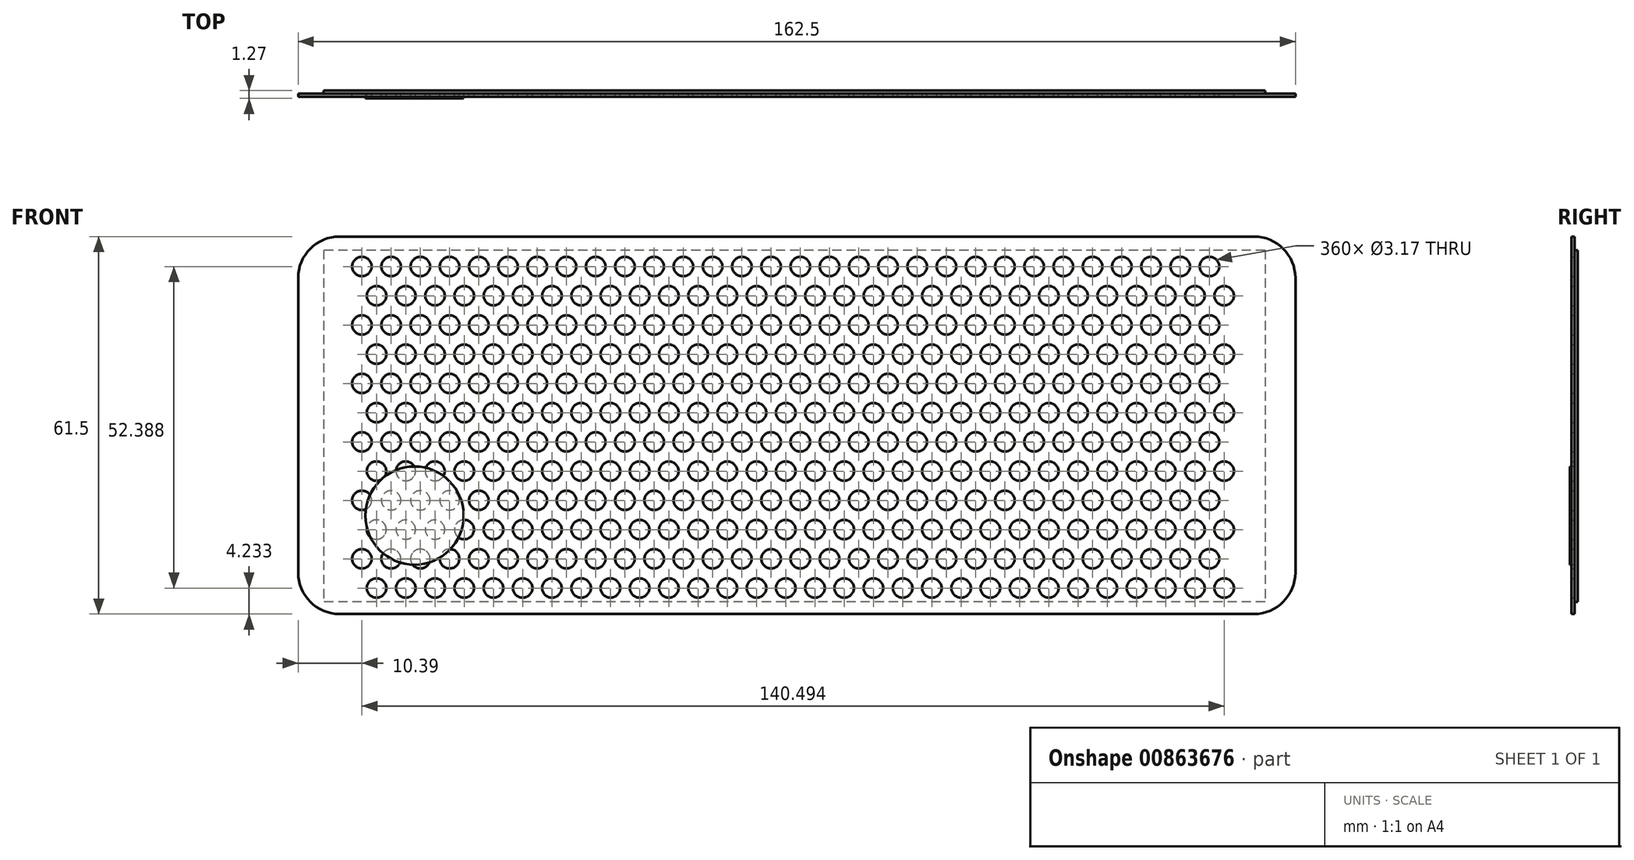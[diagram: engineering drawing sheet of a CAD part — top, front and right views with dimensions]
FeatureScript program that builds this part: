
annotation { "Feature Type Name" : "Feature", "Feature Type Description" : "" }
export const myFeature = defineFeature(function(context is Context, id is Id, definition is map)
    precondition{}
    {
        {
            var Q0;
            Q0=qCreatedBy(makeId("Front.planeOp"),FACE);
            var sketch = newSketch(context, id + "F0", { "sketchPlane" : qUnion([Q0])});
            skLineSegment(sketch, "E0.bottom", {"start": v(-73.44, 17) * mm, "end": v(75.54, 17) * mm});
            skLineSegment(sketch, "E0.top", {"start": v(-73.44, -44.5) * mm, "end": v(75.54, -44.5) * mm});
            skLineSegment(sketch, "E0.left", {"start": v(-80.2, 10.23) * mm, "end": v(-80.2, -37.75) * mm});
            skLineSegment(sketch, "E0.right", {"start": v(82.3, 10.23) * mm, "end": v(82.3, -37.75) * mm});
            skCircle(sketch, "E1", {"center": v(-69.81, 12.11) * mm, "radius": 1.59 * mm});
            skCircle(sketch, "E2.0.1.0", {"center": v(-69.81, 2.59) * mm, "radius": 1.59 * mm});
            skCircle(sketch, "E2.0.2.0", {"center": v(-69.81, -6.94) * mm, "radius": 1.59 * mm});
            skCircle(sketch, "E2.1.0.0", {"center": v(-65.05, 12.11) * mm, "radius": 1.59 * mm});
            skCircle(sketch, "E2.1.1.0", {"center": v(-65.05, 2.59) * mm, "radius": 1.59 * mm});
            skCircle(sketch, "E2.1.2.0", {"center": v(-65.05, -6.94) * mm, "radius": 1.59 * mm});
            skCircle(sketch, "E2.2.0.0", {"center": v(-60.29, 12.11) * mm, "radius": 1.59 * mm});
            skCircle(sketch, "E2.2.1.0", {"center": v(-60.29, 2.59) * mm, "radius": 1.59 * mm});
            skCircle(sketch, "E2.2.2.0", {"center": v(-60.29, -6.94) * mm, "radius": 1.59 * mm});
            skCircle(sketch, "E2.3.0.0", {"center": v(-55.52, 12.11) * mm, "radius": 1.59 * mm});
            skCircle(sketch, "E2.3.1.0", {"center": v(-55.52, 2.59) * mm, "radius": 1.59 * mm});
            skCircle(sketch, "E2.3.2.0", {"center": v(-55.52, -6.94) * mm, "radius": 1.59 * mm});
            skCircle(sketch, "E2.4.0.0", {"center": v(-50.76, 12.11) * mm, "radius": 1.59 * mm});
            skCircle(sketch, "E2.4.1.0", {"center": v(-50.76, 2.59) * mm, "radius": 1.59 * mm});
            skCircle(sketch, "E2.4.2.0", {"center": v(-50.76, -6.94) * mm, "radius": 1.59 * mm});
            skCircle(sketch, "E2.5.0.0", {"center": v(-46, 12.11) * mm, "radius": 1.59 * mm});
            skCircle(sketch, "E2.5.1.0", {"center": v(-46, 2.59) * mm, "radius": 1.59 * mm});
            skCircle(sketch, "E2.5.2.0", {"center": v(-46, -6.94) * mm, "radius": 1.59 * mm});
            skCircle(sketch, "E2.6.0.0", {"center": v(-41.24, 12.11) * mm, "radius": 1.59 * mm});
            skCircle(sketch, "E2.6.1.0", {"center": v(-41.24, 2.59) * mm, "radius": 1.59 * mm});
            skCircle(sketch, "E2.6.2.0", {"center": v(-41.24, -6.94) * mm, "radius": 1.59 * mm});
            skCircle(sketch, "E2.7.0.0", {"center": v(-36.47, 12.11) * mm, "radius": 1.59 * mm});
            skCircle(sketch, "E2.7.1.0", {"center": v(-36.47, 2.59) * mm, "radius": 1.59 * mm});
            skCircle(sketch, "E2.7.2.0", {"center": v(-36.47, -6.94) * mm, "radius": 1.59 * mm});
            skCircle(sketch, "E2.8.0.0", {"center": v(-31.71, 12.11) * mm, "radius": 1.59 * mm});
            skCircle(sketch, "E2.8.1.0", {"center": v(-31.71, 2.59) * mm, "radius": 1.59 * mm});
            skCircle(sketch, "E2.8.2.0", {"center": v(-31.71, -6.94) * mm, "radius": 1.59 * mm});
            skCircle(sketch, "E2.9.0.0", {"center": v(-26.95, 12.11) * mm, "radius": 1.59 * mm});
            skCircle(sketch, "E2.9.1.0", {"center": v(-26.95, 2.59) * mm, "radius": 1.59 * mm});
            skCircle(sketch, "E2.9.2.0", {"center": v(-26.95, -6.94) * mm, "radius": 1.59 * mm});
            skCircle(sketch, "E2.10.0.0", {"center": v(-22.19, 12.11) * mm, "radius": 1.59 * mm});
            skCircle(sketch, "E2.10.1.0", {"center": v(-22.19, 2.59) * mm, "radius": 1.59 * mm});
            skCircle(sketch, "E2.10.2.0", {"center": v(-22.19, -6.94) * mm, "radius": 1.59 * mm});
            skCircle(sketch, "E2.11.0.0", {"center": v(-17.42, 12.11) * mm, "radius": 1.59 * mm});
            skCircle(sketch, "E2.11.1.0", {"center": v(-17.42, 2.59) * mm, "radius": 1.59 * mm});
            skCircle(sketch, "E2.11.2.0", {"center": v(-17.42, -6.94) * mm, "radius": 1.59 * mm});
            skCircle(sketch, "E2.12.0.0", {"center": v(-12.66, 12.11) * mm, "radius": 1.59 * mm});
            skCircle(sketch, "E2.12.1.0", {"center": v(-12.66, 2.59) * mm, "radius": 1.59 * mm});
            skCircle(sketch, "E2.12.2.0", {"center": v(-12.66, -6.94) * mm, "radius": 1.59 * mm});
            skCircle(sketch, "E2.13.0.0", {"center": v(-7.9, 12.11) * mm, "radius": 1.59 * mm});
            skCircle(sketch, "E2.13.1.0", {"center": v(-7.9, 2.59) * mm, "radius": 1.59 * mm});
            skCircle(sketch, "E2.13.2.0", {"center": v(-7.9, -6.94) * mm, "radius": 1.59 * mm});
            skCircle(sketch, "E2.14.0.0", {"center": v(-3.14, 12.11) * mm, "radius": 1.59 * mm});
            skCircle(sketch, "E2.14.1.0", {"center": v(-3.14, 2.59) * mm, "radius": 1.59 * mm});
            skCircle(sketch, "E2.14.2.0", {"center": v(-3.14, -6.94) * mm, "radius": 1.59 * mm});
            skCircle(sketch, "E2.15.0.0", {"center": v(1.63, 12.11) * mm, "radius": 1.59 * mm});
            skCircle(sketch, "E2.15.1.0", {"center": v(1.63, 2.59) * mm, "radius": 1.59 * mm});
            skCircle(sketch, "E2.15.2.0", {"center": v(1.63, -6.94) * mm, "radius": 1.59 * mm});
            skCircle(sketch, "E2.16.0.0", {"center": v(6.39, 12.11) * mm, "radius": 1.59 * mm});
            skCircle(sketch, "E2.16.1.0", {"center": v(6.39, 2.59) * mm, "radius": 1.59 * mm});
            skCircle(sketch, "E2.16.2.0", {"center": v(6.39, -6.94) * mm, "radius": 1.59 * mm});
            skCircle(sketch, "E2.17.0.0", {"center": v(11.15, 12.11) * mm, "radius": 1.59 * mm});
            skCircle(sketch, "E2.17.1.0", {"center": v(11.15, 2.59) * mm, "radius": 1.59 * mm});
            skCircle(sketch, "E2.17.2.0", {"center": v(11.15, -6.94) * mm, "radius": 1.59 * mm});
            skCircle(sketch, "E2.18.0.0", {"center": v(15.91, 12.11) * mm, "radius": 1.59 * mm});
            skCircle(sketch, "E2.18.1.0", {"center": v(15.91, 2.59) * mm, "radius": 1.59 * mm});
            skCircle(sketch, "E2.18.2.0", {"center": v(15.91, -6.94) * mm, "radius": 1.59 * mm});
            skCircle(sketch, "E2.19.0.0", {"center": v(20.68, 12.11) * mm, "radius": 1.59 * mm});
            skCircle(sketch, "E2.19.1.0", {"center": v(20.68, 2.59) * mm, "radius": 1.59 * mm});
            skCircle(sketch, "E2.19.2.0", {"center": v(20.68, -6.94) * mm, "radius": 1.59 * mm});
            skLineSegment(sketch, "E2.direction1", {"start": v(-69.81, 12.11) * mm, "end": v(-65.05, 12.11) * mm, "construction": true});
            skLineSegment(sketch, "E2.direction2", {"start": v(-69.81, 12.11) * mm, "end": v(-69.81, 2.59) * mm, "construction": true});
            skCircle(sketch, "E3.0.20.0", {"center": v(25.44, 12.11) * mm, "radius": 1.59 * mm});
            skCircle(sketch, "E3.0.20.1", {"center": v(25.44, 2.59) * mm, "radius": 1.59 * mm});
            skCircle(sketch, "E3.0.20.2", {"center": v(25.44, -6.94) * mm, "radius": 1.59 * mm});
            skCircle(sketch, "E3.0.21.0", {"center": v(30.2, 12.11) * mm, "radius": 1.59 * mm});
            skCircle(sketch, "E3.0.21.1", {"center": v(30.2, 2.59) * mm, "radius": 1.59 * mm});
            skCircle(sketch, "E3.0.21.2", {"center": v(30.2, -6.94) * mm, "radius": 1.59 * mm});
            skCircle(sketch, "E3.0.22.0", {"center": v(34.96, 12.11) * mm, "radius": 1.59 * mm});
            skCircle(sketch, "E3.0.22.1", {"center": v(34.96, 2.59) * mm, "radius": 1.59 * mm});
            skCircle(sketch, "E3.0.22.2", {"center": v(34.96, -6.94) * mm, "radius": 1.59 * mm});
            skCircle(sketch, "E3.0.23.0", {"center": v(39.73, 12.11) * mm, "radius": 1.59 * mm});
            skCircle(sketch, "E3.0.23.1", {"center": v(39.73, 2.59) * mm, "radius": 1.59 * mm});
            skCircle(sketch, "E3.0.23.2", {"center": v(39.73, -6.94) * mm, "radius": 1.59 * mm});
            skCircle(sketch, "E3.0.24.0", {"center": v(44.49, 12.11) * mm, "radius": 1.59 * mm});
            skCircle(sketch, "E3.0.24.1", {"center": v(44.49, 2.59) * mm, "radius": 1.59 * mm});
            skCircle(sketch, "E3.0.24.2", {"center": v(44.49, -6.94) * mm, "radius": 1.59 * mm});
            skCircle(sketch, "E3.0.25.0", {"center": v(49.25, 12.11) * mm, "radius": 1.59 * mm});
            skCircle(sketch, "E3.0.25.1", {"center": v(49.25, 2.59) * mm, "radius": 1.59 * mm});
            skCircle(sketch, "E3.0.25.2", {"center": v(49.25, -6.94) * mm, "radius": 1.59 * mm});
            skCircle(sketch, "E3.0.26.0", {"center": v(54.01, 12.11) * mm, "radius": 1.59 * mm});
            skCircle(sketch, "E3.0.26.1", {"center": v(54.01, 2.59) * mm, "radius": 1.59 * mm});
            skCircle(sketch, "E3.0.26.2", {"center": v(54.01, -6.94) * mm, "radius": 1.59 * mm});
            skCircle(sketch, "E3.0.27.0", {"center": v(58.78, 12.11) * mm, "radius": 1.59 * mm});
            skCircle(sketch, "E3.0.27.1", {"center": v(58.78, 2.59) * mm, "radius": 1.59 * mm});
            skCircle(sketch, "E3.0.27.2", {"center": v(58.78, -6.94) * mm, "radius": 1.59 * mm});
            skCircle(sketch, "E3.0.28.0", {"center": v(63.54, 12.11) * mm, "radius": 1.59 * mm});
            skCircle(sketch, "E3.0.28.1", {"center": v(63.54, 2.59) * mm, "radius": 1.59 * mm});
            skCircle(sketch, "E3.0.28.2", {"center": v(63.54, -6.94) * mm, "radius": 1.59 * mm});
            skCircle(sketch, "E3.0.29.0", {"center": v(68.3, 12.11) * mm, "radius": 1.59 * mm});
            skCircle(sketch, "E3.0.29.1", {"center": v(68.3, 2.59) * mm, "radius": 1.59 * mm});
            skCircle(sketch, "E3.0.29.2", {"center": v(68.3, -6.94) * mm, "radius": 1.59 * mm});
            skCircle(sketch, "E4", {"center": v(-67.43, 7.35) * mm, "radius": 1.59 * mm});
            skLineSegment(sketch, "E5", {"start": v(-65.05, 2.59) * mm, "end": v(-69.81, 12.11) * mm});
            skCircle(sketch, "E6.0.0.3", {"center": v(-69.81, -16.46) * mm, "radius": 1.59 * mm});
            skCircle(sketch, "E6.0.0.4", {"center": v(-69.81, -25.99) * mm, "radius": 1.59 * mm});
            skCircle(sketch, "E6.0.0.5", {"center": v(-69.81, -35.51) * mm, "radius": 1.59 * mm});
            skCircle(sketch, "E6.0.1.3", {"center": v(-65.05, -16.46) * mm, "radius": 1.59 * mm});
            skCircle(sketch, "E6.0.1.4", {"center": v(-65.05, -25.99) * mm, "radius": 1.59 * mm});
            skCircle(sketch, "E6.0.1.5", {"center": v(-65.05, -35.51) * mm, "radius": 1.59 * mm});
            skCircle(sketch, "E6.0.2.3", {"center": v(-60.29, -16.46) * mm, "radius": 1.59 * mm});
            skCircle(sketch, "E6.0.2.4", {"center": v(-60.29, -25.99) * mm, "radius": 1.59 * mm});
            skCircle(sketch, "E6.0.2.5", {"center": v(-60.29, -35.51) * mm, "radius": 1.59 * mm});
            skCircle(sketch, "E6.0.3.3", {"center": v(-55.52, -16.46) * mm, "radius": 1.59 * mm});
            skCircle(sketch, "E6.0.3.4", {"center": v(-55.52, -25.99) * mm, "radius": 1.59 * mm});
            skCircle(sketch, "E6.0.3.5", {"center": v(-55.52, -35.51) * mm, "radius": 1.59 * mm});
            skCircle(sketch, "E6.0.4.3", {"center": v(-50.76, -16.46) * mm, "radius": 1.59 * mm});
            skCircle(sketch, "E6.0.4.4", {"center": v(-50.76, -25.99) * mm, "radius": 1.59 * mm});
            skCircle(sketch, "E6.0.4.5", {"center": v(-50.76, -35.51) * mm, "radius": 1.59 * mm});
            skCircle(sketch, "E6.0.5.3", {"center": v(-46, -16.46) * mm, "radius": 1.59 * mm});
            skCircle(sketch, "E6.0.5.4", {"center": v(-46, -25.99) * mm, "radius": 1.59 * mm});
            skCircle(sketch, "E6.0.5.5", {"center": v(-46, -35.51) * mm, "radius": 1.59 * mm});
            skCircle(sketch, "E6.0.6.3", {"center": v(-41.24, -16.46) * mm, "radius": 1.59 * mm});
            skCircle(sketch, "E6.0.6.4", {"center": v(-41.24, -25.99) * mm, "radius": 1.59 * mm});
            skCircle(sketch, "E6.0.6.5", {"center": v(-41.24, -35.51) * mm, "radius": 1.59 * mm});
            skCircle(sketch, "E6.0.7.3", {"center": v(-36.47, -16.46) * mm, "radius": 1.59 * mm});
            skCircle(sketch, "E6.0.7.4", {"center": v(-36.47, -25.99) * mm, "radius": 1.59 * mm});
            skCircle(sketch, "E6.0.7.5", {"center": v(-36.47, -35.51) * mm, "radius": 1.59 * mm});
            skCircle(sketch, "E6.0.8.3", {"center": v(-31.71, -16.46) * mm, "radius": 1.59 * mm});
            skCircle(sketch, "E6.0.8.4", {"center": v(-31.71, -25.99) * mm, "radius": 1.59 * mm});
            skCircle(sketch, "E6.0.8.5", {"center": v(-31.71, -35.51) * mm, "radius": 1.59 * mm});
            skCircle(sketch, "E6.0.9.3", {"center": v(-26.95, -16.46) * mm, "radius": 1.59 * mm});
            skCircle(sketch, "E6.0.9.4", {"center": v(-26.95, -25.99) * mm, "radius": 1.59 * mm});
            skCircle(sketch, "E6.0.9.5", {"center": v(-26.95, -35.51) * mm, "radius": 1.59 * mm});
            skCircle(sketch, "E6.0.10.3", {"center": v(-22.19, -16.46) * mm, "radius": 1.59 * mm});
            skCircle(sketch, "E6.0.10.4", {"center": v(-22.19, -25.99) * mm, "radius": 1.59 * mm});
            skCircle(sketch, "E6.0.10.5", {"center": v(-22.19, -35.51) * mm, "radius": 1.59 * mm});
            skCircle(sketch, "E6.0.11.3", {"center": v(-17.42, -16.46) * mm, "radius": 1.59 * mm});
            skCircle(sketch, "E6.0.11.4", {"center": v(-17.42, -25.99) * mm, "radius": 1.59 * mm});
            skCircle(sketch, "E6.0.11.5", {"center": v(-17.42, -35.51) * mm, "radius": 1.59 * mm});
            skCircle(sketch, "E6.0.12.3", {"center": v(-12.66, -16.46) * mm, "radius": 1.59 * mm});
            skCircle(sketch, "E6.0.12.4", {"center": v(-12.66, -25.99) * mm, "radius": 1.59 * mm});
            skCircle(sketch, "E6.0.12.5", {"center": v(-12.66, -35.51) * mm, "radius": 1.59 * mm});
            skCircle(sketch, "E6.0.13.3", {"center": v(-7.9, -16.46) * mm, "radius": 1.59 * mm});
            skCircle(sketch, "E6.0.13.4", {"center": v(-7.9, -25.99) * mm, "radius": 1.59 * mm});
            skCircle(sketch, "E6.0.13.5", {"center": v(-7.9, -35.51) * mm, "radius": 1.59 * mm});
            skCircle(sketch, "E6.0.14.3", {"center": v(-3.14, -16.46) * mm, "radius": 1.59 * mm});
            skCircle(sketch, "E6.0.14.4", {"center": v(-3.14, -25.99) * mm, "radius": 1.59 * mm});
            skCircle(sketch, "E6.0.14.5", {"center": v(-3.14, -35.51) * mm, "radius": 1.59 * mm});
            skCircle(sketch, "E6.0.15.3", {"center": v(1.63, -16.46) * mm, "radius": 1.59 * mm});
            skCircle(sketch, "E6.0.15.4", {"center": v(1.63, -25.99) * mm, "radius": 1.59 * mm});
            skCircle(sketch, "E6.0.15.5", {"center": v(1.63, -35.51) * mm, "radius": 1.59 * mm});
            skCircle(sketch, "E6.0.16.3", {"center": v(6.39, -16.46) * mm, "radius": 1.59 * mm});
            skCircle(sketch, "E6.0.16.4", {"center": v(6.39, -25.99) * mm, "radius": 1.59 * mm});
            skCircle(sketch, "E6.0.16.5", {"center": v(6.39, -35.51) * mm, "radius": 1.59 * mm});
            skCircle(sketch, "E6.0.17.3", {"center": v(11.15, -16.46) * mm, "radius": 1.59 * mm});
            skCircle(sketch, "E6.0.17.4", {"center": v(11.15, -25.99) * mm, "radius": 1.59 * mm});
            skCircle(sketch, "E6.0.17.5", {"center": v(11.15, -35.51) * mm, "radius": 1.59 * mm});
            skCircle(sketch, "E6.0.18.3", {"center": v(15.91, -16.46) * mm, "radius": 1.59 * mm});
            skCircle(sketch, "E6.0.18.4", {"center": v(15.91, -25.99) * mm, "radius": 1.59 * mm});
            skCircle(sketch, "E6.0.18.5", {"center": v(15.91, -35.51) * mm, "radius": 1.59 * mm});
            skCircle(sketch, "E6.0.19.3", {"center": v(20.68, -16.46) * mm, "radius": 1.59 * mm});
            skCircle(sketch, "E6.0.19.4", {"center": v(20.68, -25.99) * mm, "radius": 1.59 * mm});
            skCircle(sketch, "E6.0.19.5", {"center": v(20.68, -35.51) * mm, "radius": 1.59 * mm});
            skCircle(sketch, "E6.0.20.3", {"center": v(25.44, -16.46) * mm, "radius": 1.59 * mm});
            skCircle(sketch, "E6.0.20.4", {"center": v(25.44, -25.99) * mm, "radius": 1.59 * mm});
            skCircle(sketch, "E6.0.20.5", {"center": v(25.44, -35.51) * mm, "radius": 1.59 * mm});
            skCircle(sketch, "E6.0.21.3", {"center": v(30.2, -16.46) * mm, "radius": 1.59 * mm});
            skCircle(sketch, "E6.0.21.4", {"center": v(30.2, -25.99) * mm, "radius": 1.59 * mm});
            skCircle(sketch, "E6.0.21.5", {"center": v(30.2, -35.51) * mm, "radius": 1.59 * mm});
            skCircle(sketch, "E6.0.22.3", {"center": v(34.96, -16.46) * mm, "radius": 1.59 * mm});
            skCircle(sketch, "E6.0.22.4", {"center": v(34.96, -25.99) * mm, "radius": 1.59 * mm});
            skCircle(sketch, "E6.0.22.5", {"center": v(34.96, -35.51) * mm, "radius": 1.59 * mm});
            skCircle(sketch, "E6.0.23.3", {"center": v(39.73, -16.46) * mm, "radius": 1.59 * mm});
            skCircle(sketch, "E6.0.23.4", {"center": v(39.73, -25.99) * mm, "radius": 1.59 * mm});
            skCircle(sketch, "E6.0.23.5", {"center": v(39.73, -35.51) * mm, "radius": 1.59 * mm});
            skCircle(sketch, "E6.0.24.3", {"center": v(44.49, -16.46) * mm, "radius": 1.59 * mm});
            skCircle(sketch, "E6.0.24.4", {"center": v(44.49, -25.99) * mm, "radius": 1.59 * mm});
            skCircle(sketch, "E6.0.24.5", {"center": v(44.49, -35.51) * mm, "radius": 1.59 * mm});
            skCircle(sketch, "E6.0.25.3", {"center": v(49.25, -16.46) * mm, "radius": 1.59 * mm});
            skCircle(sketch, "E6.0.25.4", {"center": v(49.25, -25.99) * mm, "radius": 1.59 * mm});
            skCircle(sketch, "E6.0.25.5", {"center": v(49.25, -35.51) * mm, "radius": 1.59 * mm});
            skCircle(sketch, "E6.0.26.3", {"center": v(54.01, -16.46) * mm, "radius": 1.59 * mm});
            skCircle(sketch, "E6.0.26.4", {"center": v(54.01, -25.99) * mm, "radius": 1.59 * mm});
            skCircle(sketch, "E6.0.26.5", {"center": v(54.01, -35.51) * mm, "radius": 1.59 * mm});
            skCircle(sketch, "E6.0.27.3", {"center": v(58.78, -16.46) * mm, "radius": 1.59 * mm});
            skCircle(sketch, "E6.0.27.4", {"center": v(58.78, -25.99) * mm, "radius": 1.59 * mm});
            skCircle(sketch, "E6.0.27.5", {"center": v(58.78, -35.51) * mm, "radius": 1.59 * mm});
            skCircle(sketch, "E6.0.28.3", {"center": v(63.54, -16.46) * mm, "radius": 1.59 * mm});
            skCircle(sketch, "E6.0.28.4", {"center": v(63.54, -25.99) * mm, "radius": 1.59 * mm});
            skCircle(sketch, "E6.0.28.5", {"center": v(63.54, -35.51) * mm, "radius": 1.59 * mm});
            skCircle(sketch, "E6.0.29.3", {"center": v(68.3, -16.46) * mm, "radius": 1.59 * mm});
            skCircle(sketch, "E6.0.29.4", {"center": v(68.3, -25.99) * mm, "radius": 1.59 * mm});
            skCircle(sketch, "E6.0.29.5", {"center": v(68.3, -35.51) * mm, "radius": 1.59 * mm});
            skCircle(sketch, "E7.0.1.0", {"center": v(-67.43, -2.18) * mm, "radius": 1.59 * mm});
            skCircle(sketch, "E7.0.2.0", {"center": v(-67.43, -11.7) * mm, "radius": 1.59 * mm});
            skCircle(sketch, "E7.0.3.0", {"center": v(-67.43, -21.23) * mm, "radius": 1.59 * mm});
            skCircle(sketch, "E7.0.4.0", {"center": v(-67.43, -30.75) * mm, "radius": 1.59 * mm});
            skCircle(sketch, "E7.0.5.0", {"center": v(-67.43, -40.28) * mm, "radius": 1.59 * mm});
            skCircle(sketch, "E7.1.0.0", {"center": v(-62.67, 7.35) * mm, "radius": 1.59 * mm});
            skCircle(sketch, "E7.1.1.0", {"center": v(-62.67, -2.18) * mm, "radius": 1.59 * mm});
            skCircle(sketch, "E7.1.2.0", {"center": v(-62.67, -11.7) * mm, "radius": 1.59 * mm});
            skCircle(sketch, "E7.1.3.0", {"center": v(-62.67, -21.23) * mm, "radius": 1.59 * mm});
            skCircle(sketch, "E7.1.4.0", {"center": v(-62.67, -30.75) * mm, "radius": 1.59 * mm});
            skCircle(sketch, "E7.1.5.0", {"center": v(-62.67, -40.28) * mm, "radius": 1.59 * mm});
            skCircle(sketch, "E7.2.0.0", {"center": v(-57.9, 7.35) * mm, "radius": 1.59 * mm});
            skCircle(sketch, "E7.2.1.0", {"center": v(-57.9, -2.18) * mm, "radius": 1.59 * mm});
            skCircle(sketch, "E7.2.2.0", {"center": v(-57.9, -11.7) * mm, "radius": 1.59 * mm});
            skCircle(sketch, "E7.2.3.0", {"center": v(-57.9, -21.23) * mm, "radius": 1.59 * mm});
            skCircle(sketch, "E7.2.4.0", {"center": v(-57.9, -30.75) * mm, "radius": 1.59 * mm});
            skCircle(sketch, "E7.2.5.0", {"center": v(-57.9, -40.28) * mm, "radius": 1.59 * mm});
            skCircle(sketch, "E7.3.0.0", {"center": v(-53.14, 7.35) * mm, "radius": 1.59 * mm});
            skCircle(sketch, "E7.3.1.0", {"center": v(-53.14, -2.18) * mm, "radius": 1.59 * mm});
            skCircle(sketch, "E7.3.2.0", {"center": v(-53.14, -11.7) * mm, "radius": 1.59 * mm});
            skCircle(sketch, "E7.3.3.0", {"center": v(-53.14, -21.23) * mm, "radius": 1.59 * mm});
            skCircle(sketch, "E7.3.4.0", {"center": v(-53.14, -30.75) * mm, "radius": 1.59 * mm});
            skCircle(sketch, "E7.3.5.0", {"center": v(-53.14, -40.28) * mm, "radius": 1.59 * mm});
            skCircle(sketch, "E7.4.0.0", {"center": v(-48.38, 7.35) * mm, "radius": 1.59 * mm});
            skCircle(sketch, "E7.4.1.0", {"center": v(-48.38, -2.18) * mm, "radius": 1.59 * mm});
            skCircle(sketch, "E7.4.2.0", {"center": v(-48.38, -11.7) * mm, "radius": 1.59 * mm});
            skCircle(sketch, "E7.4.3.0", {"center": v(-48.38, -21.23) * mm, "radius": 1.59 * mm});
            skCircle(sketch, "E7.4.4.0", {"center": v(-48.38, -30.75) * mm, "radius": 1.59 * mm});
            skCircle(sketch, "E7.4.5.0", {"center": v(-48.38, -40.28) * mm, "radius": 1.59 * mm});
            skCircle(sketch, "E7.5.0.0", {"center": v(-43.62, 7.35) * mm, "radius": 1.59 * mm});
            skCircle(sketch, "E7.5.1.0", {"center": v(-43.62, -2.18) * mm, "radius": 1.59 * mm});
            skCircle(sketch, "E7.5.2.0", {"center": v(-43.62, -11.7) * mm, "radius": 1.59 * mm});
            skCircle(sketch, "E7.5.3.0", {"center": v(-43.62, -21.23) * mm, "radius": 1.59 * mm});
            skCircle(sketch, "E7.5.4.0", {"center": v(-43.62, -30.75) * mm, "radius": 1.59 * mm});
            skCircle(sketch, "E7.5.5.0", {"center": v(-43.62, -40.28) * mm, "radius": 1.59 * mm});
            skCircle(sketch, "E7.6.0.0", {"center": v(-38.85, 7.35) * mm, "radius": 1.59 * mm});
            skCircle(sketch, "E7.6.1.0", {"center": v(-38.85, -2.18) * mm, "radius": 1.59 * mm});
            skCircle(sketch, "E7.6.2.0", {"center": v(-38.85, -11.7) * mm, "radius": 1.59 * mm});
            skCircle(sketch, "E7.6.3.0", {"center": v(-38.85, -21.23) * mm, "radius": 1.59 * mm});
            skCircle(sketch, "E7.6.4.0", {"center": v(-38.85, -30.75) * mm, "radius": 1.59 * mm});
            skCircle(sketch, "E7.6.5.0", {"center": v(-38.85, -40.28) * mm, "radius": 1.59 * mm});
            skCircle(sketch, "E7.7.0.0", {"center": v(-34.1, 7.35) * mm, "radius": 1.59 * mm});
            skCircle(sketch, "E7.7.1.0", {"center": v(-34.1, -2.18) * mm, "radius": 1.59 * mm});
            skCircle(sketch, "E7.7.2.0", {"center": v(-34.1, -11.7) * mm, "radius": 1.59 * mm});
            skCircle(sketch, "E7.7.3.0", {"center": v(-34.1, -21.23) * mm, "radius": 1.59 * mm});
            skCircle(sketch, "E7.7.4.0", {"center": v(-34.1, -30.75) * mm, "radius": 1.59 * mm});
            skCircle(sketch, "E7.7.5.0", {"center": v(-34.1, -40.28) * mm, "radius": 1.59 * mm});
            skCircle(sketch, "E7.8.0.0", {"center": v(-29.33, 7.35) * mm, "radius": 1.59 * mm});
            skCircle(sketch, "E7.8.1.0", {"center": v(-29.33, -2.18) * mm, "radius": 1.59 * mm});
            skCircle(sketch, "E7.8.2.0", {"center": v(-29.33, -11.7) * mm, "radius": 1.59 * mm});
            skCircle(sketch, "E7.8.3.0", {"center": v(-29.33, -21.23) * mm, "radius": 1.59 * mm});
            skCircle(sketch, "E7.8.4.0", {"center": v(-29.33, -30.75) * mm, "radius": 1.59 * mm});
            skCircle(sketch, "E7.8.5.0", {"center": v(-29.33, -40.28) * mm, "radius": 1.59 * mm});
            skCircle(sketch, "E7.9.0.0", {"center": v(-24.57, 7.35) * mm, "radius": 1.59 * mm});
            skCircle(sketch, "E7.9.1.0", {"center": v(-24.57, -2.18) * mm, "radius": 1.59 * mm});
            skCircle(sketch, "E7.9.2.0", {"center": v(-24.57, -11.7) * mm, "radius": 1.59 * mm});
            skCircle(sketch, "E7.9.3.0", {"center": v(-24.57, -21.23) * mm, "radius": 1.59 * mm});
            skCircle(sketch, "E7.9.4.0", {"center": v(-24.57, -30.75) * mm, "radius": 1.59 * mm});
            skCircle(sketch, "E7.9.5.0", {"center": v(-24.57, -40.28) * mm, "radius": 1.59 * mm});
            skCircle(sketch, "E7.10.0.0", {"center": v(-19.8, 7.35) * mm, "radius": 1.59 * mm});
            skCircle(sketch, "E7.10.1.0", {"center": v(-19.8, -2.18) * mm, "radius": 1.59 * mm});
            skCircle(sketch, "E7.10.2.0", {"center": v(-19.8, -11.7) * mm, "radius": 1.59 * mm});
            skCircle(sketch, "E7.10.3.0", {"center": v(-19.8, -21.23) * mm, "radius": 1.59 * mm});
            skCircle(sketch, "E7.10.4.0", {"center": v(-19.8, -30.75) * mm, "radius": 1.59 * mm});
            skCircle(sketch, "E7.10.5.0", {"center": v(-19.8, -40.28) * mm, "radius": 1.59 * mm});
            skCircle(sketch, "E7.11.0.0", {"center": v(-15.04, 7.35) * mm, "radius": 1.59 * mm});
            skCircle(sketch, "E7.11.1.0", {"center": v(-15.04, -2.18) * mm, "radius": 1.59 * mm});
            skCircle(sketch, "E7.11.2.0", {"center": v(-15.04, -11.7) * mm, "radius": 1.59 * mm});
            skCircle(sketch, "E7.11.3.0", {"center": v(-15.04, -21.23) * mm, "radius": 1.59 * mm});
            skCircle(sketch, "E7.11.4.0", {"center": v(-15.04, -30.75) * mm, "radius": 1.59 * mm});
            skCircle(sketch, "E7.11.5.0", {"center": v(-15.04, -40.28) * mm, "radius": 1.59 * mm});
            skCircle(sketch, "E7.12.0.0", {"center": v(-10.28, 7.35) * mm, "radius": 1.59 * mm});
            skCircle(sketch, "E7.12.1.0", {"center": v(-10.28, -2.18) * mm, "radius": 1.59 * mm});
            skCircle(sketch, "E7.12.2.0", {"center": v(-10.28, -11.7) * mm, "radius": 1.59 * mm});
            skCircle(sketch, "E7.12.3.0", {"center": v(-10.28, -21.23) * mm, "radius": 1.59 * mm});
            skCircle(sketch, "E7.12.4.0", {"center": v(-10.28, -30.75) * mm, "radius": 1.59 * mm});
            skCircle(sketch, "E7.12.5.0", {"center": v(-10.28, -40.28) * mm, "radius": 1.59 * mm});
            skCircle(sketch, "E7.13.0.0", {"center": v(-5.52, 7.35) * mm, "radius": 1.59 * mm});
            skCircle(sketch, "E7.13.1.0", {"center": v(-5.52, -2.18) * mm, "radius": 1.59 * mm});
            skCircle(sketch, "E7.13.2.0", {"center": v(-5.52, -11.7) * mm, "radius": 1.59 * mm});
            skCircle(sketch, "E7.13.3.0", {"center": v(-5.52, -21.23) * mm, "radius": 1.59 * mm});
            skCircle(sketch, "E7.13.4.0", {"center": v(-5.52, -30.75) * mm, "radius": 1.59 * mm});
            skCircle(sketch, "E7.13.5.0", {"center": v(-5.52, -40.28) * mm, "radius": 1.59 * mm});
            skCircle(sketch, "E7.14.0.0", {"center": v(-0.75, 7.35) * mm, "radius": 1.59 * mm});
            skCircle(sketch, "E7.14.1.0", {"center": v(-0.75, -2.18) * mm, "radius": 1.59 * mm});
            skCircle(sketch, "E7.14.2.0", {"center": v(-0.75, -11.7) * mm, "radius": 1.59 * mm});
            skCircle(sketch, "E7.14.3.0", {"center": v(-0.75, -21.23) * mm, "radius": 1.59 * mm});
            skCircle(sketch, "E7.14.4.0", {"center": v(-0.75, -30.75) * mm, "radius": 1.59 * mm});
            skCircle(sketch, "E7.14.5.0", {"center": v(-0.75, -40.28) * mm, "radius": 1.59 * mm});
            skCircle(sketch, "E7.15.0.0", {"center": v(4, 7.35) * mm, "radius": 1.59 * mm});
            skCircle(sketch, "E7.15.1.0", {"center": v(4, -2.18) * mm, "radius": 1.59 * mm});
            skCircle(sketch, "E7.15.2.0", {"center": v(4, -11.7) * mm, "radius": 1.59 * mm});
            skCircle(sketch, "E7.15.3.0", {"center": v(4, -21.23) * mm, "radius": 1.59 * mm});
            skCircle(sketch, "E7.15.4.0", {"center": v(4, -30.75) * mm, "radius": 1.59 * mm});
            skCircle(sketch, "E7.15.5.0", {"center": v(4, -40.28) * mm, "radius": 1.59 * mm});
            skCircle(sketch, "E7.16.0.0", {"center": v(8.77, 7.35) * mm, "radius": 1.59 * mm});
            skCircle(sketch, "E7.16.1.0", {"center": v(8.77, -2.18) * mm, "radius": 1.59 * mm});
            skCircle(sketch, "E7.16.2.0", {"center": v(8.77, -11.7) * mm, "radius": 1.59 * mm});
            skCircle(sketch, "E7.16.3.0", {"center": v(8.77, -21.23) * mm, "radius": 1.59 * mm});
            skCircle(sketch, "E7.16.4.0", {"center": v(8.77, -30.75) * mm, "radius": 1.59 * mm});
            skCircle(sketch, "E7.16.5.0", {"center": v(8.77, -40.28) * mm, "radius": 1.59 * mm});
            skCircle(sketch, "E7.17.0.0", {"center": v(13.53, 7.35) * mm, "radius": 1.59 * mm});
            skCircle(sketch, "E7.17.1.0", {"center": v(13.53, -2.18) * mm, "radius": 1.59 * mm});
            skCircle(sketch, "E7.17.2.0", {"center": v(13.53, -11.7) * mm, "radius": 1.59 * mm});
            skCircle(sketch, "E7.17.3.0", {"center": v(13.53, -21.23) * mm, "radius": 1.59 * mm});
            skCircle(sketch, "E7.17.4.0", {"center": v(13.53, -30.75) * mm, "radius": 1.59 * mm});
            skCircle(sketch, "E7.17.5.0", {"center": v(13.53, -40.28) * mm, "radius": 1.59 * mm});
            skCircle(sketch, "E7.18.0.0", {"center": v(18.3, 7.35) * mm, "radius": 1.59 * mm});
            skCircle(sketch, "E7.18.1.0", {"center": v(18.3, -2.18) * mm, "radius": 1.59 * mm});
            skCircle(sketch, "E7.18.2.0", {"center": v(18.3, -11.7) * mm, "radius": 1.59 * mm});
            skCircle(sketch, "E7.18.3.0", {"center": v(18.3, -21.23) * mm, "radius": 1.59 * mm});
            skCircle(sketch, "E7.18.4.0", {"center": v(18.3, -30.75) * mm, "radius": 1.59 * mm});
            skCircle(sketch, "E7.18.5.0", {"center": v(18.3, -40.28) * mm, "radius": 1.59 * mm});
            skCircle(sketch, "E7.19.0.0", {"center": v(23.06, 7.35) * mm, "radius": 1.59 * mm});
            skCircle(sketch, "E7.19.1.0", {"center": v(23.06, -2.18) * mm, "radius": 1.59 * mm});
            skCircle(sketch, "E7.19.2.0", {"center": v(23.06, -11.7) * mm, "radius": 1.59 * mm});
            skCircle(sketch, "E7.19.3.0", {"center": v(23.06, -21.23) * mm, "radius": 1.59 * mm});
            skCircle(sketch, "E7.19.4.0", {"center": v(23.06, -30.75) * mm, "radius": 1.59 * mm});
            skCircle(sketch, "E7.19.5.0", {"center": v(23.06, -40.28) * mm, "radius": 1.59 * mm});
            skCircle(sketch, "E7.20.0.0", {"center": v(27.82, 7.35) * mm, "radius": 1.59 * mm});
            skCircle(sketch, "E7.20.1.0", {"center": v(27.82, -2.18) * mm, "radius": 1.59 * mm});
            skCircle(sketch, "E7.20.2.0", {"center": v(27.82, -11.7) * mm, "radius": 1.59 * mm});
            skCircle(sketch, "E7.20.3.0", {"center": v(27.82, -21.23) * mm, "radius": 1.59 * mm});
            skCircle(sketch, "E7.20.4.0", {"center": v(27.82, -30.75) * mm, "radius": 1.59 * mm});
            skCircle(sketch, "E7.20.5.0", {"center": v(27.82, -40.28) * mm, "radius": 1.59 * mm});
            skCircle(sketch, "E7.21.0.0", {"center": v(32.58, 7.35) * mm, "radius": 1.59 * mm});
            skCircle(sketch, "E7.21.1.0", {"center": v(32.58, -2.18) * mm, "radius": 1.59 * mm});
            skCircle(sketch, "E7.21.2.0", {"center": v(32.58, -11.7) * mm, "radius": 1.59 * mm});
            skCircle(sketch, "E7.21.3.0", {"center": v(32.58, -21.23) * mm, "radius": 1.59 * mm});
            skCircle(sketch, "E7.21.4.0", {"center": v(32.58, -30.75) * mm, "radius": 1.59 * mm});
            skCircle(sketch, "E7.21.5.0", {"center": v(32.58, -40.28) * mm, "radius": 1.59 * mm});
            skCircle(sketch, "E7.22.0.0", {"center": v(37.35, 7.35) * mm, "radius": 1.59 * mm});
            skCircle(sketch, "E7.22.1.0", {"center": v(37.35, -2.18) * mm, "radius": 1.59 * mm});
            skCircle(sketch, "E7.22.2.0", {"center": v(37.35, -11.7) * mm, "radius": 1.59 * mm});
            skCircle(sketch, "E7.22.3.0", {"center": v(37.35, -21.23) * mm, "radius": 1.59 * mm});
            skCircle(sketch, "E7.22.4.0", {"center": v(37.35, -30.75) * mm, "radius": 1.59 * mm});
            skCircle(sketch, "E7.22.5.0", {"center": v(37.35, -40.28) * mm, "radius": 1.59 * mm});
            skCircle(sketch, "E7.23.0.0", {"center": v(42.1, 7.35) * mm, "radius": 1.59 * mm});
            skCircle(sketch, "E7.23.1.0", {"center": v(42.1, -2.18) * mm, "radius": 1.59 * mm});
            skCircle(sketch, "E7.23.2.0", {"center": v(42.1, -11.7) * mm, "radius": 1.59 * mm});
            skCircle(sketch, "E7.23.3.0", {"center": v(42.1, -21.23) * mm, "radius": 1.59 * mm});
            skCircle(sketch, "E7.23.4.0", {"center": v(42.1, -30.75) * mm, "radius": 1.59 * mm});
            skCircle(sketch, "E7.23.5.0", {"center": v(42.1, -40.28) * mm, "radius": 1.59 * mm});
            skCircle(sketch, "E7.24.0.0", {"center": v(46.87, 7.35) * mm, "radius": 1.59 * mm});
            skCircle(sketch, "E7.24.1.0", {"center": v(46.87, -2.18) * mm, "radius": 1.59 * mm});
            skCircle(sketch, "E7.24.2.0", {"center": v(46.87, -11.7) * mm, "radius": 1.59 * mm});
            skCircle(sketch, "E7.24.3.0", {"center": v(46.87, -21.23) * mm, "radius": 1.59 * mm});
            skCircle(sketch, "E7.24.4.0", {"center": v(46.87, -30.75) * mm, "radius": 1.59 * mm});
            skCircle(sketch, "E7.24.5.0", {"center": v(46.87, -40.28) * mm, "radius": 1.59 * mm});
            skCircle(sketch, "E7.25.0.0", {"center": v(51.63, 7.35) * mm, "radius": 1.59 * mm});
            skCircle(sketch, "E7.25.1.0", {"center": v(51.63, -2.18) * mm, "radius": 1.59 * mm});
            skCircle(sketch, "E7.25.2.0", {"center": v(51.63, -11.7) * mm, "radius": 1.59 * mm});
            skCircle(sketch, "E7.25.3.0", {"center": v(51.63, -21.23) * mm, "radius": 1.59 * mm});
            skCircle(sketch, "E7.25.4.0", {"center": v(51.63, -30.75) * mm, "radius": 1.59 * mm});
            skCircle(sketch, "E7.25.5.0", {"center": v(51.63, -40.28) * mm, "radius": 1.59 * mm});
            skCircle(sketch, "E7.26.0.0", {"center": v(56.4, 7.35) * mm, "radius": 1.59 * mm});
            skCircle(sketch, "E7.26.1.0", {"center": v(56.4, -2.18) * mm, "radius": 1.59 * mm});
            skCircle(sketch, "E7.26.2.0", {"center": v(56.4, -11.7) * mm, "radius": 1.59 * mm});
            skCircle(sketch, "E7.26.3.0", {"center": v(56.4, -21.23) * mm, "radius": 1.59 * mm});
            skCircle(sketch, "E7.26.4.0", {"center": v(56.4, -30.75) * mm, "radius": 1.59 * mm});
            skCircle(sketch, "E7.26.5.0", {"center": v(56.4, -40.28) * mm, "radius": 1.59 * mm});
            skCircle(sketch, "E7.27.0.0", {"center": v(61.16, 7.35) * mm, "radius": 1.59 * mm});
            skCircle(sketch, "E7.27.1.0", {"center": v(61.16, -2.18) * mm, "radius": 1.59 * mm});
            skCircle(sketch, "E7.27.2.0", {"center": v(61.16, -11.7) * mm, "radius": 1.59 * mm});
            skCircle(sketch, "E7.27.3.0", {"center": v(61.16, -21.23) * mm, "radius": 1.59 * mm});
            skCircle(sketch, "E7.27.4.0", {"center": v(61.16, -30.75) * mm, "radius": 1.59 * mm});
            skCircle(sketch, "E7.27.5.0", {"center": v(61.16, -40.28) * mm, "radius": 1.59 * mm});
            skCircle(sketch, "E7.28.0.0", {"center": v(65.92, 7.35) * mm, "radius": 1.59 * mm});
            skCircle(sketch, "E7.28.1.0", {"center": v(65.92, -2.18) * mm, "radius": 1.59 * mm});
            skCircle(sketch, "E7.28.2.0", {"center": v(65.92, -11.7) * mm, "radius": 1.59 * mm});
            skCircle(sketch, "E7.28.3.0", {"center": v(65.92, -21.23) * mm, "radius": 1.59 * mm});
            skCircle(sketch, "E7.28.4.0", {"center": v(65.92, -30.75) * mm, "radius": 1.59 * mm});
            skCircle(sketch, "E7.28.5.0", {"center": v(65.92, -40.28) * mm, "radius": 1.59 * mm});
            skCircle(sketch, "E7.29.0.0", {"center": v(70.68, 7.35) * mm, "radius": 1.59 * mm});
            skCircle(sketch, "E7.29.1.0", {"center": v(70.68, -2.18) * mm, "radius": 1.59 * mm});
            skCircle(sketch, "E7.29.2.0", {"center": v(70.68, -11.7) * mm, "radius": 1.59 * mm});
            skCircle(sketch, "E7.29.3.0", {"center": v(70.68, -21.23) * mm, "radius": 1.59 * mm});
            skCircle(sketch, "E7.29.4.0", {"center": v(70.68, -30.75) * mm, "radius": 1.59 * mm});
            skCircle(sketch, "E7.29.5.0", {"center": v(70.68, -40.28) * mm, "radius": 1.59 * mm});
            skLineSegment(sketch, "E7.direction1", {"start": v(-67.43, 7.35) * mm, "end": v(-62.67, 7.35) * mm, "construction": true});
            skLineSegment(sketch, "E7.direction2", {"start": v(-67.43, 7.35) * mm, "end": v(-67.43, -2.18) * mm, "construction": true});
            skPoint(sketch, "E8.visualSharp", {"position": v(-80.2, 17) * mm});
            skArc(sketch, "E8.filletArc", {"start": v(-73.44, 17) * mm, "mid": v(-78.22, 15.01) * mm, "end": v(-80.2, 10.23) * mm});
            skPoint(sketch, "E9.visualSharp", {"position": v(-80.2, -44.5) * mm});
            skArc(sketch, "E9.filletArc", {"start": v(-80.2, -37.75) * mm, "mid": v(-78.22, -42.53) * mm, "end": v(-73.44, -44.5) * mm});
            skPoint(sketch, "E10.visualSharp", {"position": v(82.3, 17) * mm});
            skArc(sketch, "E10.filletArc", {"start": v(82.3, 10.23) * mm, "mid": v(80.32, 15.01) * mm, "end": v(75.54, 17) * mm});
            skPoint(sketch, "E11.visualSharp", {"position": v(82.3, -44.5) * mm});
            skArc(sketch, "E11.filletArc", {"start": v(75.54, -44.5) * mm, "mid": v(80.32, -42.53) * mm, "end": v(82.3, -37.75) * mm});
            skSolve(sketch);
        }
        {
            var Q0;
            Q0=qSketchRegion(id+"F0",true);
            extrude(context, id + "F1", {"entities" : qUnion([Q0]), "depth" : 0.5 * mm, "offsetDistance" : 25.4 * mm});
        }
        {
            var Q0;
            Q0=makeQuery(id+"F1.opExtrude","CAP_FACE",FACE,{"disambiguationData":[OSD([sQuery(id+"F0.wireOp",EDGE,"E0.bottom"),sQuery(id+"F0.wireOp",EDGE,"E0.top"),sQuery(id+"F0.wireOp",EDGE,"E0.left"),sQuery(id+"F0.wireOp",EDGE,"E0.right"),sQuery(id+"F0.wireOp",EDGE,"E1"),sQuery(id+"F0.wireOp",EDGE,"E2.0.1.0"),sQuery(id+"F0.wireOp",EDGE,"E2.0.2.0"),sQuery(id+"F0.wireOp",EDGE,"E2.1.0.0"),sQuery(id+"F0.wireOp",EDGE,"E2.1.1.0"),sQuery(id+"F0.wireOp",EDGE,"E2.1.2.0"),sQuery(id+"F0.wireOp",EDGE,"E2.2.0.0"),sQuery(id+"F0.wireOp",EDGE,"E2.2.1.0"),sQuery(id+"F0.wireOp",EDGE,"E2.2.2.0"),sQuery(id+"F0.wireOp",EDGE,"E2.3.0.0"),sQuery(id+"F0.wireOp",EDGE,"E2.3.1.0"),sQuery(id+"F0.wireOp",EDGE,"E2.3.2.0"),sQuery(id+"F0.wireOp",EDGE,"E2.4.0.0"),sQuery(id+"F0.wireOp",EDGE,"E2.4.1.0"),sQuery(id+"F0.wireOp",EDGE,"E2.4.2.0"),sQuery(id+"F0.wireOp",EDGE,"E2.5.0.0"),sQuery(id+"F0.wireOp",EDGE,"E2.5.1.0"),sQuery(id+"F0.wireOp",EDGE,"E2.5.2.0"),sQuery(id+"F0.wireOp",EDGE,"E2.6.0.0"),sQuery(id+"F0.wireOp",EDGE,"E2.6.1.0"),sQuery(id+"F0.wireOp",EDGE,"E2.6.2.0"),sQuery(id+"F0.wireOp",EDGE,"E2.7.0.0"),sQuery(id+"F0.wireOp",EDGE,"E2.7.1.0"),sQuery(id+"F0.wireOp",EDGE,"E2.7.2.0"),sQuery(id+"F0.wireOp",EDGE,"E2.8.0.0"),sQuery(id+"F0.wireOp",EDGE,"E2.8.1.0"),sQuery(id+"F0.wireOp",EDGE,"E2.8.2.0"),sQuery(id+"F0.wireOp",EDGE,"E2.9.0.0"),sQuery(id+"F0.wireOp",EDGE,"E2.9.1.0"),sQuery(id+"F0.wireOp",EDGE,"E2.9.2.0"),sQuery(id+"F0.wireOp",EDGE,"E2.10.0.0"),sQuery(id+"F0.wireOp",EDGE,"E2.10.1.0"),sQuery(id+"F0.wireOp",EDGE,"E2.10.2.0"),sQuery(id+"F0.wireOp",EDGE,"E2.11.0.0"),sQuery(id+"F0.wireOp",EDGE,"E2.11.1.0"),sQuery(id+"F0.wireOp",EDGE,"E2.11.2.0"),sQuery(id+"F0.wireOp",EDGE,"E2.12.0.0"),sQuery(id+"F0.wireOp",EDGE,"E2.12.1.0"),sQuery(id+"F0.wireOp",EDGE,"E2.12.2.0"),sQuery(id+"F0.wireOp",EDGE,"E2.13.0.0"),sQuery(id+"F0.wireOp",EDGE,"E2.13.1.0"),sQuery(id+"F0.wireOp",EDGE,"E2.13.2.0"),sQuery(id+"F0.wireOp",EDGE,"E2.14.0.0"),sQuery(id+"F0.wireOp",EDGE,"E2.14.1.0"),sQuery(id+"F0.wireOp",EDGE,"E2.14.2.0"),sQuery(id+"F0.wireOp",EDGE,"E2.15.0.0"),sQuery(id+"F0.wireOp",EDGE,"E2.15.1.0"),sQuery(id+"F0.wireOp",EDGE,"E2.15.2.0"),sQuery(id+"F0.wireOp",EDGE,"E2.16.0.0"),sQuery(id+"F0.wireOp",EDGE,"E2.16.1.0"),sQuery(id+"F0.wireOp",EDGE,"E2.16.2.0"),sQuery(id+"F0.wireOp",EDGE,"E2.17.0.0"),sQuery(id+"F0.wireOp",EDGE,"E2.17.1.0"),sQuery(id+"F0.wireOp",EDGE,"E2.17.2.0"),sQuery(id+"F0.wireOp",EDGE,"E2.18.0.0"),sQuery(id+"F0.wireOp",EDGE,"E2.18.1.0"),sQuery(id+"F0.wireOp",EDGE,"E2.18.2.0"),sQuery(id+"F0.wireOp",EDGE,"E2.19.0.0"),sQuery(id+"F0.wireOp",EDGE,"E2.19.1.0"),sQuery(id+"F0.wireOp",EDGE,"E2.19.2.0"),sQuery(id+"F0.wireOp",EDGE,"E3.0.20.0"),sQuery(id+"F0.wireOp",EDGE,"E3.0.20.1"),sQuery(id+"F0.wireOp",EDGE,"E3.0.20.2"),sQuery(id+"F0.wireOp",EDGE,"E3.0.21.0"),sQuery(id+"F0.wireOp",EDGE,"E3.0.21.1"),sQuery(id+"F0.wireOp",EDGE,"E3.0.21.2"),sQuery(id+"F0.wireOp",EDGE,"E3.0.22.0"),sQuery(id+"F0.wireOp",EDGE,"E3.0.22.1"),sQuery(id+"F0.wireOp",EDGE,"E3.0.22.2"),sQuery(id+"F0.wireOp",EDGE,"E3.0.23.0"),sQuery(id+"F0.wireOp",EDGE,"E3.0.23.1"),sQuery(id+"F0.wireOp",EDGE,"E3.0.23.2"),sQuery(id+"F0.wireOp",EDGE,"E3.0.24.0"),sQuery(id+"F0.wireOp",EDGE,"E3.0.24.1"),sQuery(id+"F0.wireOp",EDGE,"E3.0.24.2"),sQuery(id+"F0.wireOp",EDGE,"E3.0.25.0"),sQuery(id+"F0.wireOp",EDGE,"E3.0.25.1"),sQuery(id+"F0.wireOp",EDGE,"E3.0.25.2"),sQuery(id+"F0.wireOp",EDGE,"E3.0.26.0"),sQuery(id+"F0.wireOp",EDGE,"E3.0.26.1"),sQuery(id+"F0.wireOp",EDGE,"E3.0.26.2"),sQuery(id+"F0.wireOp",EDGE,"E3.0.27.0"),sQuery(id+"F0.wireOp",EDGE,"E3.0.27.1"),sQuery(id+"F0.wireOp",EDGE,"E3.0.27.2"),sQuery(id+"F0.wireOp",EDGE,"E3.0.28.0"),sQuery(id+"F0.wireOp",EDGE,"E3.0.28.1"),sQuery(id+"F0.wireOp",EDGE,"E3.0.28.2"),sQuery(id+"F0.wireOp",EDGE,"E3.0.29.0"),sQuery(id+"F0.wireOp",EDGE,"E3.0.29.1"),sQuery(id+"F0.wireOp",EDGE,"E3.0.29.2"),sQuery(id+"F0.wireOp",EDGE,"E4"),sQuery(id+"F0.wireOp",EDGE,"E6.0.0.3"),sQuery(id+"F0.wireOp",EDGE,"E6.0.0.4"),sQuery(id+"F0.wireOp",EDGE,"E6.0.0.5"),sQuery(id+"F0.wireOp",EDGE,"E6.0.1.3"),sQuery(id+"F0.wireOp",EDGE,"E6.0.1.4"),sQuery(id+"F0.wireOp",EDGE,"E6.0.1.5"),sQuery(id+"F0.wireOp",EDGE,"E6.0.2.3"),sQuery(id+"F0.wireOp",EDGE,"E6.0.2.4"),sQuery(id+"F0.wireOp",EDGE,"E6.0.2.5"),sQuery(id+"F0.wireOp",EDGE,"E6.0.3.3"),sQuery(id+"F0.wireOp",EDGE,"E6.0.3.4"),sQuery(id+"F0.wireOp",EDGE,"E6.0.3.5"),sQuery(id+"F0.wireOp",EDGE,"E6.0.4.3"),sQuery(id+"F0.wireOp",EDGE,"E6.0.4.4"),sQuery(id+"F0.wireOp",EDGE,"E6.0.4.5"),sQuery(id+"F0.wireOp",EDGE,"E6.0.5.3"),sQuery(id+"F0.wireOp",EDGE,"E6.0.5.4"),sQuery(id+"F0.wireOp",EDGE,"E6.0.5.5"),sQuery(id+"F0.wireOp",EDGE,"E6.0.6.3"),sQuery(id+"F0.wireOp",EDGE,"E6.0.6.4"),sQuery(id+"F0.wireOp",EDGE,"E6.0.6.5"),sQuery(id+"F0.wireOp",EDGE,"E6.0.7.3"),sQuery(id+"F0.wireOp",EDGE,"E6.0.7.4"),sQuery(id+"F0.wireOp",EDGE,"E6.0.7.5"),sQuery(id+"F0.wireOp",EDGE,"E6.0.8.3"),sQuery(id+"F0.wireOp",EDGE,"E6.0.8.4"),sQuery(id+"F0.wireOp",EDGE,"E6.0.8.5"),sQuery(id+"F0.wireOp",EDGE,"E6.0.9.3"),sQuery(id+"F0.wireOp",EDGE,"E6.0.9.4"),sQuery(id+"F0.wireOp",EDGE,"E6.0.9.5"),sQuery(id+"F0.wireOp",EDGE,"E6.0.10.3"),sQuery(id+"F0.wireOp",EDGE,"E6.0.10.4"),sQuery(id+"F0.wireOp",EDGE,"E6.0.10.5"),sQuery(id+"F0.wireOp",EDGE,"E6.0.11.3"),sQuery(id+"F0.wireOp",EDGE,"E6.0.11.4"),sQuery(id+"F0.wireOp",EDGE,"E6.0.11.5"),sQuery(id+"F0.wireOp",EDGE,"E6.0.12.3"),sQuery(id+"F0.wireOp",EDGE,"E6.0.12.4"),sQuery(id+"F0.wireOp",EDGE,"E6.0.12.5"),sQuery(id+"F0.wireOp",EDGE,"E6.0.13.3"),sQuery(id+"F0.wireOp",EDGE,"E6.0.13.4"),sQuery(id+"F0.wireOp",EDGE,"E6.0.13.5"),sQuery(id+"F0.wireOp",EDGE,"E6.0.14.3"),sQuery(id+"F0.wireOp",EDGE,"E6.0.14.4"),sQuery(id+"F0.wireOp",EDGE,"E6.0.14.5"),sQuery(id+"F0.wireOp",EDGE,"E6.0.15.3"),sQuery(id+"F0.wireOp",EDGE,"E6.0.15.4"),sQuery(id+"F0.wireOp",EDGE,"E6.0.15.5"),sQuery(id+"F0.wireOp",EDGE,"E6.0.16.3"),sQuery(id+"F0.wireOp",EDGE,"E6.0.16.4"),sQuery(id+"F0.wireOp",EDGE,"E6.0.16.5"),sQuery(id+"F0.wireOp",EDGE,"E6.0.17.3"),sQuery(id+"F0.wireOp",EDGE,"E6.0.17.4"),sQuery(id+"F0.wireOp",EDGE,"E6.0.17.5"),sQuery(id+"F0.wireOp",EDGE,"E6.0.18.3"),sQuery(id+"F0.wireOp",EDGE,"E6.0.18.4"),sQuery(id+"F0.wireOp",EDGE,"E6.0.18.5"),sQuery(id+"F0.wireOp",EDGE,"E6.0.19.3"),sQuery(id+"F0.wireOp",EDGE,"E6.0.19.4"),sQuery(id+"F0.wireOp",EDGE,"E6.0.19.5"),sQuery(id+"F0.wireOp",EDGE,"E6.0.20.3"),sQuery(id+"F0.wireOp",EDGE,"E6.0.20.4"),sQuery(id+"F0.wireOp",EDGE,"E6.0.20.5"),sQuery(id+"F0.wireOp",EDGE,"E6.0.21.3"),sQuery(id+"F0.wireOp",EDGE,"E6.0.21.4"),sQuery(id+"F0.wireOp",EDGE,"E6.0.21.5"),sQuery(id+"F0.wireOp",EDGE,"E6.0.22.3"),sQuery(id+"F0.wireOp",EDGE,"E6.0.22.4"),sQuery(id+"F0.wireOp",EDGE,"E6.0.22.5"),sQuery(id+"F0.wireOp",EDGE,"E6.0.23.3"),sQuery(id+"F0.wireOp",EDGE,"E6.0.23.4"),sQuery(id+"F0.wireOp",EDGE,"E6.0.23.5"),sQuery(id+"F0.wireOp",EDGE,"E6.0.24.3"),sQuery(id+"F0.wireOp",EDGE,"E6.0.24.4"),sQuery(id+"F0.wireOp",EDGE,"E6.0.24.5"),sQuery(id+"F0.wireOp",EDGE,"E6.0.25.3"),sQuery(id+"F0.wireOp",EDGE,"E6.0.25.4"),sQuery(id+"F0.wireOp",EDGE,"E6.0.25.5"),sQuery(id+"F0.wireOp",EDGE,"E6.0.26.3"),sQuery(id+"F0.wireOp",EDGE,"E6.0.26.4"),sQuery(id+"F0.wireOp",EDGE,"E6.0.26.5"),sQuery(id+"F0.wireOp",EDGE,"E6.0.27.3"),sQuery(id+"F0.wireOp",EDGE,"E6.0.27.4"),sQuery(id+"F0.wireOp",EDGE,"E6.0.27.5"),sQuery(id+"F0.wireOp",EDGE,"E6.0.28.3"),sQuery(id+"F0.wireOp",EDGE,"E6.0.28.4"),sQuery(id+"F0.wireOp",EDGE,"E6.0.28.5"),sQuery(id+"F0.wireOp",EDGE,"E6.0.29.3"),sQuery(id+"F0.wireOp",EDGE,"E6.0.29.4"),sQuery(id+"F0.wireOp",EDGE,"E6.0.29.5"),sQuery(id+"F0.wireOp",EDGE,"E7.0.1.0"),sQuery(id+"F0.wireOp",EDGE,"E7.0.2.0"),sQuery(id+"F0.wireOp",EDGE,"E7.0.3.0"),sQuery(id+"F0.wireOp",EDGE,"E7.0.4.0"),sQuery(id+"F0.wireOp",EDGE,"E7.0.5.0"),sQuery(id+"F0.wireOp",EDGE,"E7.1.0.0"),sQuery(id+"F0.wireOp",EDGE,"E7.1.1.0"),sQuery(id+"F0.wireOp",EDGE,"E7.1.2.0"),sQuery(id+"F0.wireOp",EDGE,"E7.1.3.0"),sQuery(id+"F0.wireOp",EDGE,"E7.1.4.0"),sQuery(id+"F0.wireOp",EDGE,"E7.1.5.0"),sQuery(id+"F0.wireOp",EDGE,"E7.2.0.0"),sQuery(id+"F0.wireOp",EDGE,"E7.2.1.0"),sQuery(id+"F0.wireOp",EDGE,"E7.2.2.0"),sQuery(id+"F0.wireOp",EDGE,"E7.2.3.0"),sQuery(id+"F0.wireOp",EDGE,"E7.2.4.0"),sQuery(id+"F0.wireOp",EDGE,"E7.2.5.0"),sQuery(id+"F0.wireOp",EDGE,"E7.3.0.0"),sQuery(id+"F0.wireOp",EDGE,"E7.3.1.0"),sQuery(id+"F0.wireOp",EDGE,"E7.3.2.0"),sQuery(id+"F0.wireOp",EDGE,"E7.3.3.0"),sQuery(id+"F0.wireOp",EDGE,"E7.3.4.0"),sQuery(id+"F0.wireOp",EDGE,"E7.3.5.0"),sQuery(id+"F0.wireOp",EDGE,"E7.4.0.0"),sQuery(id+"F0.wireOp",EDGE,"E7.4.1.0"),sQuery(id+"F0.wireOp",EDGE,"E7.4.2.0"),sQuery(id+"F0.wireOp",EDGE,"E7.4.3.0"),sQuery(id+"F0.wireOp",EDGE,"E7.4.4.0"),sQuery(id+"F0.wireOp",EDGE,"E7.4.5.0"),sQuery(id+"F0.wireOp",EDGE,"E7.5.0.0"),sQuery(id+"F0.wireOp",EDGE,"E7.5.1.0"),sQuery(id+"F0.wireOp",EDGE,"E7.5.2.0"),sQuery(id+"F0.wireOp",EDGE,"E7.5.3.0"),sQuery(id+"F0.wireOp",EDGE,"E7.5.4.0"),sQuery(id+"F0.wireOp",EDGE,"E7.5.5.0"),sQuery(id+"F0.wireOp",EDGE,"E7.6.0.0"),sQuery(id+"F0.wireOp",EDGE,"E7.6.1.0"),sQuery(id+"F0.wireOp",EDGE,"E7.6.2.0"),sQuery(id+"F0.wireOp",EDGE,"E7.6.3.0"),sQuery(id+"F0.wireOp",EDGE,"E7.6.4.0"),sQuery(id+"F0.wireOp",EDGE,"E7.6.5.0"),sQuery(id+"F0.wireOp",EDGE,"E7.7.0.0"),sQuery(id+"F0.wireOp",EDGE,"E7.7.1.0"),sQuery(id+"F0.wireOp",EDGE,"E7.7.2.0"),sQuery(id+"F0.wireOp",EDGE,"E7.7.3.0"),sQuery(id+"F0.wireOp",EDGE,"E7.7.4.0"),sQuery(id+"F0.wireOp",EDGE,"E7.7.5.0"),sQuery(id+"F0.wireOp",EDGE,"E7.8.0.0"),sQuery(id+"F0.wireOp",EDGE,"E7.8.1.0"),sQuery(id+"F0.wireOp",EDGE,"E7.8.2.0"),sQuery(id+"F0.wireOp",EDGE,"E7.8.3.0"),sQuery(id+"F0.wireOp",EDGE,"E7.8.4.0"),sQuery(id+"F0.wireOp",EDGE,"E7.8.5.0"),sQuery(id+"F0.wireOp",EDGE,"E7.9.0.0"),sQuery(id+"F0.wireOp",EDGE,"E7.9.1.0"),sQuery(id+"F0.wireOp",EDGE,"E7.9.2.0"),sQuery(id+"F0.wireOp",EDGE,"E7.9.3.0"),sQuery(id+"F0.wireOp",EDGE,"E7.9.4.0"),sQuery(id+"F0.wireOp",EDGE,"E7.9.5.0"),sQuery(id+"F0.wireOp",EDGE,"E7.10.0.0"),sQuery(id+"F0.wireOp",EDGE,"E7.10.1.0"),sQuery(id+"F0.wireOp",EDGE,"E7.10.2.0"),sQuery(id+"F0.wireOp",EDGE,"E7.10.3.0"),sQuery(id+"F0.wireOp",EDGE,"E7.10.4.0"),sQuery(id+"F0.wireOp",EDGE,"E7.10.5.0"),sQuery(id+"F0.wireOp",EDGE,"E7.11.0.0"),sQuery(id+"F0.wireOp",EDGE,"E7.11.1.0"),sQuery(id+"F0.wireOp",EDGE,"E7.11.2.0"),sQuery(id+"F0.wireOp",EDGE,"E7.11.3.0"),sQuery(id+"F0.wireOp",EDGE,"E7.11.4.0"),sQuery(id+"F0.wireOp",EDGE,"E7.11.5.0"),sQuery(id+"F0.wireOp",EDGE,"E7.12.0.0"),sQuery(id+"F0.wireOp",EDGE,"E7.12.1.0"),sQuery(id+"F0.wireOp",EDGE,"E7.12.2.0"),sQuery(id+"F0.wireOp",EDGE,"E7.12.3.0"),sQuery(id+"F0.wireOp",EDGE,"E7.12.4.0"),sQuery(id+"F0.wireOp",EDGE,"E7.12.5.0"),sQuery(id+"F0.wireOp",EDGE,"E7.13.0.0"),sQuery(id+"F0.wireOp",EDGE,"E7.13.1.0"),sQuery(id+"F0.wireOp",EDGE,"E7.13.2.0"),sQuery(id+"F0.wireOp",EDGE,"E7.13.3.0"),sQuery(id+"F0.wireOp",EDGE,"E7.13.4.0"),sQuery(id+"F0.wireOp",EDGE,"E7.13.5.0"),sQuery(id+"F0.wireOp",EDGE,"E7.14.0.0"),sQuery(id+"F0.wireOp",EDGE,"E7.14.1.0"),sQuery(id+"F0.wireOp",EDGE,"E7.14.2.0"),sQuery(id+"F0.wireOp",EDGE,"E7.14.3.0"),sQuery(id+"F0.wireOp",EDGE,"E7.14.4.0"),sQuery(id+"F0.wireOp",EDGE,"E7.14.5.0"),sQuery(id+"F0.wireOp",EDGE,"E7.15.0.0"),sQuery(id+"F0.wireOp",EDGE,"E7.15.1.0"),sQuery(id+"F0.wireOp",EDGE,"E7.15.2.0"),sQuery(id+"F0.wireOp",EDGE,"E7.15.3.0"),sQuery(id+"F0.wireOp",EDGE,"E7.15.4.0"),sQuery(id+"F0.wireOp",EDGE,"E7.15.5.0"),sQuery(id+"F0.wireOp",EDGE,"E7.16.0.0"),sQuery(id+"F0.wireOp",EDGE,"E7.16.1.0"),sQuery(id+"F0.wireOp",EDGE,"E7.16.2.0"),sQuery(id+"F0.wireOp",EDGE,"E7.16.3.0"),sQuery(id+"F0.wireOp",EDGE,"E7.16.4.0"),sQuery(id+"F0.wireOp",EDGE,"E7.16.5.0"),sQuery(id+"F0.wireOp",EDGE,"E7.17.0.0"),sQuery(id+"F0.wireOp",EDGE,"E7.17.1.0"),sQuery(id+"F0.wireOp",EDGE,"E7.17.2.0"),sQuery(id+"F0.wireOp",EDGE,"E7.17.3.0"),sQuery(id+"F0.wireOp",EDGE,"E7.17.4.0"),sQuery(id+"F0.wireOp",EDGE,"E7.17.5.0"),sQuery(id+"F0.wireOp",EDGE,"E7.18.0.0"),sQuery(id+"F0.wireOp",EDGE,"E7.18.1.0"),sQuery(id+"F0.wireOp",EDGE,"E7.18.2.0"),sQuery(id+"F0.wireOp",EDGE,"E7.18.3.0"),sQuery(id+"F0.wireOp",EDGE,"E7.18.4.0"),sQuery(id+"F0.wireOp",EDGE,"E7.18.5.0"),sQuery(id+"F0.wireOp",EDGE,"E7.19.0.0"),sQuery(id+"F0.wireOp",EDGE,"E7.19.1.0"),sQuery(id+"F0.wireOp",EDGE,"E7.19.2.0"),sQuery(id+"F0.wireOp",EDGE,"E7.19.3.0"),sQuery(id+"F0.wireOp",EDGE,"E7.19.4.0"),sQuery(id+"F0.wireOp",EDGE,"E7.19.5.0"),sQuery(id+"F0.wireOp",EDGE,"E7.20.0.0"),sQuery(id+"F0.wireOp",EDGE,"E7.20.1.0"),sQuery(id+"F0.wireOp",EDGE,"E7.20.2.0"),sQuery(id+"F0.wireOp",EDGE,"E7.20.3.0"),sQuery(id+"F0.wireOp",EDGE,"E7.20.4.0"),sQuery(id+"F0.wireOp",EDGE,"E7.20.5.0"),sQuery(id+"F0.wireOp",EDGE,"E7.21.0.0"),sQuery(id+"F0.wireOp",EDGE,"E7.21.1.0"),sQuery(id+"F0.wireOp",EDGE,"E7.21.2.0"),sQuery(id+"F0.wireOp",EDGE,"E7.21.3.0"),sQuery(id+"F0.wireOp",EDGE,"E7.21.4.0"),sQuery(id+"F0.wireOp",EDGE,"E7.21.5.0"),sQuery(id+"F0.wireOp",EDGE,"E7.22.0.0"),sQuery(id+"F0.wireOp",EDGE,"E7.22.1.0"),sQuery(id+"F0.wireOp",EDGE,"E7.22.2.0"),sQuery(id+"F0.wireOp",EDGE,"E7.22.3.0"),sQuery(id+"F0.wireOp",EDGE,"E7.22.4.0"),sQuery(id+"F0.wireOp",EDGE,"E7.22.5.0"),sQuery(id+"F0.wireOp",EDGE,"E7.23.0.0"),sQuery(id+"F0.wireOp",EDGE,"E7.23.1.0"),sQuery(id+"F0.wireOp",EDGE,"E7.23.2.0"),sQuery(id+"F0.wireOp",EDGE,"E7.23.3.0"),sQuery(id+"F0.wireOp",EDGE,"E7.23.4.0"),sQuery(id+"F0.wireOp",EDGE,"E7.23.5.0"),sQuery(id+"F0.wireOp",EDGE,"E7.24.0.0"),sQuery(id+"F0.wireOp",EDGE,"E7.24.1.0"),sQuery(id+"F0.wireOp",EDGE,"E7.24.2.0"),sQuery(id+"F0.wireOp",EDGE,"E7.24.3.0"),sQuery(id+"F0.wireOp",EDGE,"E7.24.4.0"),sQuery(id+"F0.wireOp",EDGE,"E7.24.5.0"),sQuery(id+"F0.wireOp",EDGE,"E7.25.0.0"),sQuery(id+"F0.wireOp",EDGE,"E7.25.1.0"),sQuery(id+"F0.wireOp",EDGE,"E7.25.2.0"),sQuery(id+"F0.wireOp",EDGE,"E7.25.3.0"),sQuery(id+"F0.wireOp",EDGE,"E7.25.4.0"),sQuery(id+"F0.wireOp",EDGE,"E7.25.5.0"),sQuery(id+"F0.wireOp",EDGE,"E7.26.0.0"),sQuery(id+"F0.wireOp",EDGE,"E7.26.1.0"),sQuery(id+"F0.wireOp",EDGE,"E7.26.2.0"),sQuery(id+"F0.wireOp",EDGE,"E7.26.3.0"),sQuery(id+"F0.wireOp",EDGE,"E7.26.4.0"),sQuery(id+"F0.wireOp",EDGE,"E7.26.5.0"),sQuery(id+"F0.wireOp",EDGE,"E7.27.0.0"),sQuery(id+"F0.wireOp",EDGE,"E7.27.1.0"),sQuery(id+"F0.wireOp",EDGE,"E7.27.2.0"),sQuery(id+"F0.wireOp",EDGE,"E7.27.3.0"),sQuery(id+"F0.wireOp",EDGE,"E7.27.4.0"),sQuery(id+"F0.wireOp",EDGE,"E7.27.5.0"),sQuery(id+"F0.wireOp",EDGE,"E7.28.0.0"),sQuery(id+"F0.wireOp",EDGE,"E7.28.1.0"),sQuery(id+"F0.wireOp",EDGE,"E7.28.2.0"),sQuery(id+"F0.wireOp",EDGE,"E7.28.3.0"),sQuery(id+"F0.wireOp",EDGE,"E7.28.4.0"),sQuery(id+"F0.wireOp",EDGE,"E7.28.5.0"),sQuery(id+"F0.wireOp",EDGE,"E7.29.0.0"),sQuery(id+"F0.wireOp",EDGE,"E7.29.1.0"),sQuery(id+"F0.wireOp",EDGE,"E7.29.2.0"),sQuery(id+"F0.wireOp",EDGE,"E7.29.3.0"),sQuery(id+"F0.wireOp",EDGE,"E7.29.4.0"),sQuery(id+"F0.wireOp",EDGE,"E7.29.5.0")])],"isStart":true});
            var sketch = newSketch(context, id + "F2", { "sketchPlane" : qUnion([Q0])});
            skPoint(sketch, "E12.oppositeSnap0", {"position": v(78.22, -42.53) * mm});
            skLineSegment(sketch, "E12.bottom", {"start": v(-77.35, 14.76) * mm, "end": v(76.07, 14.76) * mm});
            skLineSegment(sketch, "E12.top", {"start": v(-77.35, -42.53) * mm, "end": v(76.07, -42.53) * mm});
            skLineSegment(sketch, "E12.left", {"start": v(-77.35, 14.76) * mm, "end": v(-77.35, -42.53) * mm});
            skLineSegment(sketch, "E12.right", {"start": v(76.07, 14.76) * mm, "end": v(76.07, -42.53) * mm});
            skSolve(sketch);
        }
        {
            var Q0;
            Q0 = qSketchRegion(id + "F2", true);
            extrude(context, id + "F3", {"entities" : qUnion([Q0]), "depth" : 0.5 * mm, "offsetDistance" : 25.4 * mm});
        }
        {
            var Q0;
            Q0=makeQuery(id+"F1.opExtrude","CAP_FACE",FACE,{"disambiguationData":[OSD([sQuery(id+"F0.wireOp",EDGE,"E0.bottom"),sQuery(id+"F0.wireOp",EDGE,"E0.top"),sQuery(id+"F0.wireOp",EDGE,"E0.left"),sQuery(id+"F0.wireOp",EDGE,"E0.right"),sQuery(id+"F0.wireOp",EDGE,"E1"),sQuery(id+"F0.wireOp",EDGE,"E2.0.1.0"),sQuery(id+"F0.wireOp",EDGE,"E2.0.2.0"),sQuery(id+"F0.wireOp",EDGE,"E2.1.0.0"),sQuery(id+"F0.wireOp",EDGE,"E2.1.1.0"),sQuery(id+"F0.wireOp",EDGE,"E2.1.2.0"),sQuery(id+"F0.wireOp",EDGE,"E2.2.0.0"),sQuery(id+"F0.wireOp",EDGE,"E2.2.1.0"),sQuery(id+"F0.wireOp",EDGE,"E2.2.2.0"),sQuery(id+"F0.wireOp",EDGE,"E2.3.0.0"),sQuery(id+"F0.wireOp",EDGE,"E2.3.1.0"),sQuery(id+"F0.wireOp",EDGE,"E2.3.2.0"),sQuery(id+"F0.wireOp",EDGE,"E2.4.0.0"),sQuery(id+"F0.wireOp",EDGE,"E2.4.1.0"),sQuery(id+"F0.wireOp",EDGE,"E2.4.2.0"),sQuery(id+"F0.wireOp",EDGE,"E2.5.0.0"),sQuery(id+"F0.wireOp",EDGE,"E2.5.1.0"),sQuery(id+"F0.wireOp",EDGE,"E2.5.2.0"),sQuery(id+"F0.wireOp",EDGE,"E2.6.0.0"),sQuery(id+"F0.wireOp",EDGE,"E2.6.1.0"),sQuery(id+"F0.wireOp",EDGE,"E2.6.2.0"),sQuery(id+"F0.wireOp",EDGE,"E2.7.0.0"),sQuery(id+"F0.wireOp",EDGE,"E2.7.1.0"),sQuery(id+"F0.wireOp",EDGE,"E2.7.2.0"),sQuery(id+"F0.wireOp",EDGE,"E2.8.0.0"),sQuery(id+"F0.wireOp",EDGE,"E2.8.1.0"),sQuery(id+"F0.wireOp",EDGE,"E2.8.2.0"),sQuery(id+"F0.wireOp",EDGE,"E2.9.0.0"),sQuery(id+"F0.wireOp",EDGE,"E2.9.1.0"),sQuery(id+"F0.wireOp",EDGE,"E2.9.2.0"),sQuery(id+"F0.wireOp",EDGE,"E2.10.0.0"),sQuery(id+"F0.wireOp",EDGE,"E2.10.1.0"),sQuery(id+"F0.wireOp",EDGE,"E2.10.2.0"),sQuery(id+"F0.wireOp",EDGE,"E2.11.0.0"),sQuery(id+"F0.wireOp",EDGE,"E2.11.1.0"),sQuery(id+"F0.wireOp",EDGE,"E2.11.2.0"),sQuery(id+"F0.wireOp",EDGE,"E2.12.0.0"),sQuery(id+"F0.wireOp",EDGE,"E2.12.1.0"),sQuery(id+"F0.wireOp",EDGE,"E2.12.2.0"),sQuery(id+"F0.wireOp",EDGE,"E2.13.0.0"),sQuery(id+"F0.wireOp",EDGE,"E2.13.1.0"),sQuery(id+"F0.wireOp",EDGE,"E2.13.2.0"),sQuery(id+"F0.wireOp",EDGE,"E2.14.0.0"),sQuery(id+"F0.wireOp",EDGE,"E2.14.1.0"),sQuery(id+"F0.wireOp",EDGE,"E2.14.2.0"),sQuery(id+"F0.wireOp",EDGE,"E2.15.0.0"),sQuery(id+"F0.wireOp",EDGE,"E2.15.1.0"),sQuery(id+"F0.wireOp",EDGE,"E2.15.2.0"),sQuery(id+"F0.wireOp",EDGE,"E2.16.0.0"),sQuery(id+"F0.wireOp",EDGE,"E2.16.1.0"),sQuery(id+"F0.wireOp",EDGE,"E2.16.2.0"),sQuery(id+"F0.wireOp",EDGE,"E2.17.0.0"),sQuery(id+"F0.wireOp",EDGE,"E2.17.1.0"),sQuery(id+"F0.wireOp",EDGE,"E2.17.2.0"),sQuery(id+"F0.wireOp",EDGE,"E2.18.0.0"),sQuery(id+"F0.wireOp",EDGE,"E2.18.1.0"),sQuery(id+"F0.wireOp",EDGE,"E2.18.2.0"),sQuery(id+"F0.wireOp",EDGE,"E2.19.0.0"),sQuery(id+"F0.wireOp",EDGE,"E2.19.1.0"),sQuery(id+"F0.wireOp",EDGE,"E2.19.2.0"),sQuery(id+"F0.wireOp",EDGE,"E3.0.20.0"),sQuery(id+"F0.wireOp",EDGE,"E3.0.20.1"),sQuery(id+"F0.wireOp",EDGE,"E3.0.20.2"),sQuery(id+"F0.wireOp",EDGE,"E3.0.21.0"),sQuery(id+"F0.wireOp",EDGE,"E3.0.21.1"),sQuery(id+"F0.wireOp",EDGE,"E3.0.21.2"),sQuery(id+"F0.wireOp",EDGE,"E3.0.22.0"),sQuery(id+"F0.wireOp",EDGE,"E3.0.22.1"),sQuery(id+"F0.wireOp",EDGE,"E3.0.22.2"),sQuery(id+"F0.wireOp",EDGE,"E3.0.23.0"),sQuery(id+"F0.wireOp",EDGE,"E3.0.23.1"),sQuery(id+"F0.wireOp",EDGE,"E3.0.23.2"),sQuery(id+"F0.wireOp",EDGE,"E3.0.24.0"),sQuery(id+"F0.wireOp",EDGE,"E3.0.24.1"),sQuery(id+"F0.wireOp",EDGE,"E3.0.24.2"),sQuery(id+"F0.wireOp",EDGE,"E3.0.25.0"),sQuery(id+"F0.wireOp",EDGE,"E3.0.25.1"),sQuery(id+"F0.wireOp",EDGE,"E3.0.25.2"),sQuery(id+"F0.wireOp",EDGE,"E3.0.26.0"),sQuery(id+"F0.wireOp",EDGE,"E3.0.26.1"),sQuery(id+"F0.wireOp",EDGE,"E3.0.26.2"),sQuery(id+"F0.wireOp",EDGE,"E3.0.27.0"),sQuery(id+"F0.wireOp",EDGE,"E3.0.27.1"),sQuery(id+"F0.wireOp",EDGE,"E3.0.27.2"),sQuery(id+"F0.wireOp",EDGE,"E3.0.28.0"),sQuery(id+"F0.wireOp",EDGE,"E3.0.28.1"),sQuery(id+"F0.wireOp",EDGE,"E3.0.28.2"),sQuery(id+"F0.wireOp",EDGE,"E3.0.29.0"),sQuery(id+"F0.wireOp",EDGE,"E3.0.29.1"),sQuery(id+"F0.wireOp",EDGE,"E3.0.29.2"),sQuery(id+"F0.wireOp",EDGE,"E4"),sQuery(id+"F0.wireOp",EDGE,"E6.0.0.3"),sQuery(id+"F0.wireOp",EDGE,"E6.0.0.4"),sQuery(id+"F0.wireOp",EDGE,"E6.0.0.5"),sQuery(id+"F0.wireOp",EDGE,"E6.0.1.3"),sQuery(id+"F0.wireOp",EDGE,"E6.0.1.4"),sQuery(id+"F0.wireOp",EDGE,"E6.0.1.5"),sQuery(id+"F0.wireOp",EDGE,"E6.0.2.3"),sQuery(id+"F0.wireOp",EDGE,"E6.0.2.4"),sQuery(id+"F0.wireOp",EDGE,"E6.0.2.5"),sQuery(id+"F0.wireOp",EDGE,"E6.0.3.3"),sQuery(id+"F0.wireOp",EDGE,"E6.0.3.4"),sQuery(id+"F0.wireOp",EDGE,"E6.0.3.5"),sQuery(id+"F0.wireOp",EDGE,"E6.0.4.3"),sQuery(id+"F0.wireOp",EDGE,"E6.0.4.4"),sQuery(id+"F0.wireOp",EDGE,"E6.0.4.5"),sQuery(id+"F0.wireOp",EDGE,"E6.0.5.3"),sQuery(id+"F0.wireOp",EDGE,"E6.0.5.4"),sQuery(id+"F0.wireOp",EDGE,"E6.0.5.5"),sQuery(id+"F0.wireOp",EDGE,"E6.0.6.3"),sQuery(id+"F0.wireOp",EDGE,"E6.0.6.4"),sQuery(id+"F0.wireOp",EDGE,"E6.0.6.5"),sQuery(id+"F0.wireOp",EDGE,"E6.0.7.3"),sQuery(id+"F0.wireOp",EDGE,"E6.0.7.4"),sQuery(id+"F0.wireOp",EDGE,"E6.0.7.5"),sQuery(id+"F0.wireOp",EDGE,"E6.0.8.3"),sQuery(id+"F0.wireOp",EDGE,"E6.0.8.4"),sQuery(id+"F0.wireOp",EDGE,"E6.0.8.5"),sQuery(id+"F0.wireOp",EDGE,"E6.0.9.3"),sQuery(id+"F0.wireOp",EDGE,"E6.0.9.4"),sQuery(id+"F0.wireOp",EDGE,"E6.0.9.5"),sQuery(id+"F0.wireOp",EDGE,"E6.0.10.3"),sQuery(id+"F0.wireOp",EDGE,"E6.0.10.4"),sQuery(id+"F0.wireOp",EDGE,"E6.0.10.5"),sQuery(id+"F0.wireOp",EDGE,"E6.0.11.3"),sQuery(id+"F0.wireOp",EDGE,"E6.0.11.4"),sQuery(id+"F0.wireOp",EDGE,"E6.0.11.5"),sQuery(id+"F0.wireOp",EDGE,"E6.0.12.3"),sQuery(id+"F0.wireOp",EDGE,"E6.0.12.4"),sQuery(id+"F0.wireOp",EDGE,"E6.0.12.5"),sQuery(id+"F0.wireOp",EDGE,"E6.0.13.3"),sQuery(id+"F0.wireOp",EDGE,"E6.0.13.4"),sQuery(id+"F0.wireOp",EDGE,"E6.0.13.5"),sQuery(id+"F0.wireOp",EDGE,"E6.0.14.3"),sQuery(id+"F0.wireOp",EDGE,"E6.0.14.4"),sQuery(id+"F0.wireOp",EDGE,"E6.0.14.5"),sQuery(id+"F0.wireOp",EDGE,"E6.0.15.3"),sQuery(id+"F0.wireOp",EDGE,"E6.0.15.4"),sQuery(id+"F0.wireOp",EDGE,"E6.0.15.5"),sQuery(id+"F0.wireOp",EDGE,"E6.0.16.3"),sQuery(id+"F0.wireOp",EDGE,"E6.0.16.4"),sQuery(id+"F0.wireOp",EDGE,"E6.0.16.5"),sQuery(id+"F0.wireOp",EDGE,"E6.0.17.3"),sQuery(id+"F0.wireOp",EDGE,"E6.0.17.4"),sQuery(id+"F0.wireOp",EDGE,"E6.0.17.5"),sQuery(id+"F0.wireOp",EDGE,"E6.0.18.3"),sQuery(id+"F0.wireOp",EDGE,"E6.0.18.4"),sQuery(id+"F0.wireOp",EDGE,"E6.0.18.5"),sQuery(id+"F0.wireOp",EDGE,"E6.0.19.3"),sQuery(id+"F0.wireOp",EDGE,"E6.0.19.4"),sQuery(id+"F0.wireOp",EDGE,"E6.0.19.5"),sQuery(id+"F0.wireOp",EDGE,"E6.0.20.3"),sQuery(id+"F0.wireOp",EDGE,"E6.0.20.4"),sQuery(id+"F0.wireOp",EDGE,"E6.0.20.5"),sQuery(id+"F0.wireOp",EDGE,"E6.0.21.3"),sQuery(id+"F0.wireOp",EDGE,"E6.0.21.4"),sQuery(id+"F0.wireOp",EDGE,"E6.0.21.5"),sQuery(id+"F0.wireOp",EDGE,"E6.0.22.3"),sQuery(id+"F0.wireOp",EDGE,"E6.0.22.4"),sQuery(id+"F0.wireOp",EDGE,"E6.0.22.5"),sQuery(id+"F0.wireOp",EDGE,"E6.0.23.3"),sQuery(id+"F0.wireOp",EDGE,"E6.0.23.4"),sQuery(id+"F0.wireOp",EDGE,"E6.0.23.5"),sQuery(id+"F0.wireOp",EDGE,"E6.0.24.3"),sQuery(id+"F0.wireOp",EDGE,"E6.0.24.4"),sQuery(id+"F0.wireOp",EDGE,"E6.0.24.5"),sQuery(id+"F0.wireOp",EDGE,"E6.0.25.3"),sQuery(id+"F0.wireOp",EDGE,"E6.0.25.4"),sQuery(id+"F0.wireOp",EDGE,"E6.0.25.5"),sQuery(id+"F0.wireOp",EDGE,"E6.0.26.3"),sQuery(id+"F0.wireOp",EDGE,"E6.0.26.4"),sQuery(id+"F0.wireOp",EDGE,"E6.0.26.5"),sQuery(id+"F0.wireOp",EDGE,"E6.0.27.3"),sQuery(id+"F0.wireOp",EDGE,"E6.0.27.4"),sQuery(id+"F0.wireOp",EDGE,"E6.0.27.5"),sQuery(id+"F0.wireOp",EDGE,"E6.0.28.3"),sQuery(id+"F0.wireOp",EDGE,"E6.0.28.4"),sQuery(id+"F0.wireOp",EDGE,"E6.0.28.5"),sQuery(id+"F0.wireOp",EDGE,"E6.0.29.3"),sQuery(id+"F0.wireOp",EDGE,"E6.0.29.4"),sQuery(id+"F0.wireOp",EDGE,"E6.0.29.5"),sQuery(id+"F0.wireOp",EDGE,"E7.0.1.0"),sQuery(id+"F0.wireOp",EDGE,"E7.0.2.0"),sQuery(id+"F0.wireOp",EDGE,"E7.0.3.0"),sQuery(id+"F0.wireOp",EDGE,"E7.0.4.0"),sQuery(id+"F0.wireOp",EDGE,"E7.0.5.0"),sQuery(id+"F0.wireOp",EDGE,"E7.1.0.0"),sQuery(id+"F0.wireOp",EDGE,"E7.1.1.0"),sQuery(id+"F0.wireOp",EDGE,"E7.1.2.0"),sQuery(id+"F0.wireOp",EDGE,"E7.1.3.0"),sQuery(id+"F0.wireOp",EDGE,"E7.1.4.0"),sQuery(id+"F0.wireOp",EDGE,"E7.1.5.0"),sQuery(id+"F0.wireOp",EDGE,"E7.2.0.0"),sQuery(id+"F0.wireOp",EDGE,"E7.2.1.0"),sQuery(id+"F0.wireOp",EDGE,"E7.2.2.0"),sQuery(id+"F0.wireOp",EDGE,"E7.2.3.0"),sQuery(id+"F0.wireOp",EDGE,"E7.2.4.0"),sQuery(id+"F0.wireOp",EDGE,"E7.2.5.0"),sQuery(id+"F0.wireOp",EDGE,"E7.3.0.0"),sQuery(id+"F0.wireOp",EDGE,"E7.3.1.0"),sQuery(id+"F0.wireOp",EDGE,"E7.3.2.0"),sQuery(id+"F0.wireOp",EDGE,"E7.3.3.0"),sQuery(id+"F0.wireOp",EDGE,"E7.3.4.0"),sQuery(id+"F0.wireOp",EDGE,"E7.3.5.0"),sQuery(id+"F0.wireOp",EDGE,"E7.4.0.0"),sQuery(id+"F0.wireOp",EDGE,"E7.4.1.0"),sQuery(id+"F0.wireOp",EDGE,"E7.4.2.0"),sQuery(id+"F0.wireOp",EDGE,"E7.4.3.0"),sQuery(id+"F0.wireOp",EDGE,"E7.4.4.0"),sQuery(id+"F0.wireOp",EDGE,"E7.4.5.0"),sQuery(id+"F0.wireOp",EDGE,"E7.5.0.0"),sQuery(id+"F0.wireOp",EDGE,"E7.5.1.0"),sQuery(id+"F0.wireOp",EDGE,"E7.5.2.0"),sQuery(id+"F0.wireOp",EDGE,"E7.5.3.0"),sQuery(id+"F0.wireOp",EDGE,"E7.5.4.0"),sQuery(id+"F0.wireOp",EDGE,"E7.5.5.0"),sQuery(id+"F0.wireOp",EDGE,"E7.6.0.0"),sQuery(id+"F0.wireOp",EDGE,"E7.6.1.0"),sQuery(id+"F0.wireOp",EDGE,"E7.6.2.0"),sQuery(id+"F0.wireOp",EDGE,"E7.6.3.0"),sQuery(id+"F0.wireOp",EDGE,"E7.6.4.0"),sQuery(id+"F0.wireOp",EDGE,"E7.6.5.0"),sQuery(id+"F0.wireOp",EDGE,"E7.7.0.0"),sQuery(id+"F0.wireOp",EDGE,"E7.7.1.0"),sQuery(id+"F0.wireOp",EDGE,"E7.7.2.0"),sQuery(id+"F0.wireOp",EDGE,"E7.7.3.0"),sQuery(id+"F0.wireOp",EDGE,"E7.7.4.0"),sQuery(id+"F0.wireOp",EDGE,"E7.7.5.0"),sQuery(id+"F0.wireOp",EDGE,"E7.8.0.0"),sQuery(id+"F0.wireOp",EDGE,"E7.8.1.0"),sQuery(id+"F0.wireOp",EDGE,"E7.8.2.0"),sQuery(id+"F0.wireOp",EDGE,"E7.8.3.0"),sQuery(id+"F0.wireOp",EDGE,"E7.8.4.0"),sQuery(id+"F0.wireOp",EDGE,"E7.8.5.0"),sQuery(id+"F0.wireOp",EDGE,"E7.9.0.0"),sQuery(id+"F0.wireOp",EDGE,"E7.9.1.0"),sQuery(id+"F0.wireOp",EDGE,"E7.9.2.0"),sQuery(id+"F0.wireOp",EDGE,"E7.9.3.0"),sQuery(id+"F0.wireOp",EDGE,"E7.9.4.0"),sQuery(id+"F0.wireOp",EDGE,"E7.9.5.0"),sQuery(id+"F0.wireOp",EDGE,"E7.10.0.0"),sQuery(id+"F0.wireOp",EDGE,"E7.10.1.0"),sQuery(id+"F0.wireOp",EDGE,"E7.10.2.0"),sQuery(id+"F0.wireOp",EDGE,"E7.10.3.0"),sQuery(id+"F0.wireOp",EDGE,"E7.10.4.0"),sQuery(id+"F0.wireOp",EDGE,"E7.10.5.0"),sQuery(id+"F0.wireOp",EDGE,"E7.11.0.0"),sQuery(id+"F0.wireOp",EDGE,"E7.11.1.0"),sQuery(id+"F0.wireOp",EDGE,"E7.11.2.0"),sQuery(id+"F0.wireOp",EDGE,"E7.11.3.0"),sQuery(id+"F0.wireOp",EDGE,"E7.11.4.0"),sQuery(id+"F0.wireOp",EDGE,"E7.11.5.0"),sQuery(id+"F0.wireOp",EDGE,"E7.12.0.0"),sQuery(id+"F0.wireOp",EDGE,"E7.12.1.0"),sQuery(id+"F0.wireOp",EDGE,"E7.12.2.0"),sQuery(id+"F0.wireOp",EDGE,"E7.12.3.0"),sQuery(id+"F0.wireOp",EDGE,"E7.12.4.0"),sQuery(id+"F0.wireOp",EDGE,"E7.12.5.0"),sQuery(id+"F0.wireOp",EDGE,"E7.13.0.0"),sQuery(id+"F0.wireOp",EDGE,"E7.13.1.0"),sQuery(id+"F0.wireOp",EDGE,"E7.13.2.0"),sQuery(id+"F0.wireOp",EDGE,"E7.13.3.0"),sQuery(id+"F0.wireOp",EDGE,"E7.13.4.0"),sQuery(id+"F0.wireOp",EDGE,"E7.13.5.0"),sQuery(id+"F0.wireOp",EDGE,"E7.14.0.0"),sQuery(id+"F0.wireOp",EDGE,"E7.14.1.0"),sQuery(id+"F0.wireOp",EDGE,"E7.14.2.0"),sQuery(id+"F0.wireOp",EDGE,"E7.14.3.0"),sQuery(id+"F0.wireOp",EDGE,"E7.14.4.0"),sQuery(id+"F0.wireOp",EDGE,"E7.14.5.0"),sQuery(id+"F0.wireOp",EDGE,"E7.15.0.0"),sQuery(id+"F0.wireOp",EDGE,"E7.15.1.0"),sQuery(id+"F0.wireOp",EDGE,"E7.15.2.0"),sQuery(id+"F0.wireOp",EDGE,"E7.15.3.0"),sQuery(id+"F0.wireOp",EDGE,"E7.15.4.0"),sQuery(id+"F0.wireOp",EDGE,"E7.15.5.0"),sQuery(id+"F0.wireOp",EDGE,"E7.16.0.0"),sQuery(id+"F0.wireOp",EDGE,"E7.16.1.0"),sQuery(id+"F0.wireOp",EDGE,"E7.16.2.0"),sQuery(id+"F0.wireOp",EDGE,"E7.16.3.0"),sQuery(id+"F0.wireOp",EDGE,"E7.16.4.0"),sQuery(id+"F0.wireOp",EDGE,"E7.16.5.0"),sQuery(id+"F0.wireOp",EDGE,"E7.17.0.0"),sQuery(id+"F0.wireOp",EDGE,"E7.17.1.0"),sQuery(id+"F0.wireOp",EDGE,"E7.17.2.0"),sQuery(id+"F0.wireOp",EDGE,"E7.17.3.0"),sQuery(id+"F0.wireOp",EDGE,"E7.17.4.0"),sQuery(id+"F0.wireOp",EDGE,"E7.17.5.0"),sQuery(id+"F0.wireOp",EDGE,"E7.18.0.0"),sQuery(id+"F0.wireOp",EDGE,"E7.18.1.0"),sQuery(id+"F0.wireOp",EDGE,"E7.18.2.0"),sQuery(id+"F0.wireOp",EDGE,"E7.18.3.0"),sQuery(id+"F0.wireOp",EDGE,"E7.18.4.0"),sQuery(id+"F0.wireOp",EDGE,"E7.18.5.0"),sQuery(id+"F0.wireOp",EDGE,"E7.19.0.0"),sQuery(id+"F0.wireOp",EDGE,"E7.19.1.0"),sQuery(id+"F0.wireOp",EDGE,"E7.19.2.0"),sQuery(id+"F0.wireOp",EDGE,"E7.19.3.0"),sQuery(id+"F0.wireOp",EDGE,"E7.19.4.0"),sQuery(id+"F0.wireOp",EDGE,"E7.19.5.0"),sQuery(id+"F0.wireOp",EDGE,"E7.20.0.0"),sQuery(id+"F0.wireOp",EDGE,"E7.20.1.0"),sQuery(id+"F0.wireOp",EDGE,"E7.20.2.0"),sQuery(id+"F0.wireOp",EDGE,"E7.20.3.0"),sQuery(id+"F0.wireOp",EDGE,"E7.20.4.0"),sQuery(id+"F0.wireOp",EDGE,"E7.20.5.0"),sQuery(id+"F0.wireOp",EDGE,"E7.21.0.0"),sQuery(id+"F0.wireOp",EDGE,"E7.21.1.0"),sQuery(id+"F0.wireOp",EDGE,"E7.21.2.0"),sQuery(id+"F0.wireOp",EDGE,"E7.21.3.0"),sQuery(id+"F0.wireOp",EDGE,"E7.21.4.0"),sQuery(id+"F0.wireOp",EDGE,"E7.21.5.0"),sQuery(id+"F0.wireOp",EDGE,"E7.22.0.0"),sQuery(id+"F0.wireOp",EDGE,"E7.22.1.0"),sQuery(id+"F0.wireOp",EDGE,"E7.22.2.0"),sQuery(id+"F0.wireOp",EDGE,"E7.22.3.0"),sQuery(id+"F0.wireOp",EDGE,"E7.22.4.0"),sQuery(id+"F0.wireOp",EDGE,"E7.22.5.0"),sQuery(id+"F0.wireOp",EDGE,"E7.23.0.0"),sQuery(id+"F0.wireOp",EDGE,"E7.23.1.0"),sQuery(id+"F0.wireOp",EDGE,"E7.23.2.0"),sQuery(id+"F0.wireOp",EDGE,"E7.23.3.0"),sQuery(id+"F0.wireOp",EDGE,"E7.23.4.0"),sQuery(id+"F0.wireOp",EDGE,"E7.23.5.0"),sQuery(id+"F0.wireOp",EDGE,"E7.24.0.0"),sQuery(id+"F0.wireOp",EDGE,"E7.24.1.0"),sQuery(id+"F0.wireOp",EDGE,"E7.24.2.0"),sQuery(id+"F0.wireOp",EDGE,"E7.24.3.0"),sQuery(id+"F0.wireOp",EDGE,"E7.24.4.0"),sQuery(id+"F0.wireOp",EDGE,"E7.24.5.0"),sQuery(id+"F0.wireOp",EDGE,"E7.25.0.0"),sQuery(id+"F0.wireOp",EDGE,"E7.25.1.0"),sQuery(id+"F0.wireOp",EDGE,"E7.25.2.0"),sQuery(id+"F0.wireOp",EDGE,"E7.25.3.0"),sQuery(id+"F0.wireOp",EDGE,"E7.25.4.0"),sQuery(id+"F0.wireOp",EDGE,"E7.25.5.0"),sQuery(id+"F0.wireOp",EDGE,"E7.26.0.0"),sQuery(id+"F0.wireOp",EDGE,"E7.26.1.0"),sQuery(id+"F0.wireOp",EDGE,"E7.26.2.0"),sQuery(id+"F0.wireOp",EDGE,"E7.26.3.0"),sQuery(id+"F0.wireOp",EDGE,"E7.26.4.0"),sQuery(id+"F0.wireOp",EDGE,"E7.26.5.0"),sQuery(id+"F0.wireOp",EDGE,"E7.27.0.0"),sQuery(id+"F0.wireOp",EDGE,"E7.27.1.0"),sQuery(id+"F0.wireOp",EDGE,"E7.27.2.0"),sQuery(id+"F0.wireOp",EDGE,"E7.27.3.0"),sQuery(id+"F0.wireOp",EDGE,"E7.27.4.0"),sQuery(id+"F0.wireOp",EDGE,"E7.27.5.0"),sQuery(id+"F0.wireOp",EDGE,"E7.28.0.0"),sQuery(id+"F0.wireOp",EDGE,"E7.28.1.0"),sQuery(id+"F0.wireOp",EDGE,"E7.28.2.0"),sQuery(id+"F0.wireOp",EDGE,"E7.28.3.0"),sQuery(id+"F0.wireOp",EDGE,"E7.28.4.0"),sQuery(id+"F0.wireOp",EDGE,"E7.28.5.0"),sQuery(id+"F0.wireOp",EDGE,"E7.29.0.0"),sQuery(id+"F0.wireOp",EDGE,"E7.29.1.0"),sQuery(id+"F0.wireOp",EDGE,"E7.29.2.0"),sQuery(id+"F0.wireOp",EDGE,"E7.29.3.0"),sQuery(id+"F0.wireOp",EDGE,"E7.29.4.0"),sQuery(id+"F0.wireOp",EDGE,"E7.29.5.0"),sQuery(id+"F0.wireOp",EDGE,"E8.filletArc"),sQuery(id+"F0.wireOp",EDGE,"E9.filletArc"),sQuery(id+"F0.wireOp",EDGE,"E10.filletArc"),sQuery(id+"F0.wireOp",EDGE,"E11.filletArc")])],"isStart":false});
            var sketch = newSketch(context, id + "F4", { "sketchPlane" : qUnion([Q0])});
            skCircle(sketch, "E13", {"center": v(-61.23, -28.47) * mm, "radius": 8 * mm});
            skSolve(sketch);
        }
        {
            var Q0;
            Q0 = qSketchRegion(id + "F4", true);
            extrude(context, id + "F5", {"entities" : qUnion([Q0]), "endBound" : BoundingType.UP_TO_NEXT, "oppositeDirection" : true, "depth" : 25.4 * mm, "offsetDistance" : 25.4 * mm, "hasSecondDirection" : true, "secondDirectionOppositeDirection" : false, "secondDirectionDepth" : 0.25 * mm});
        }
    });
